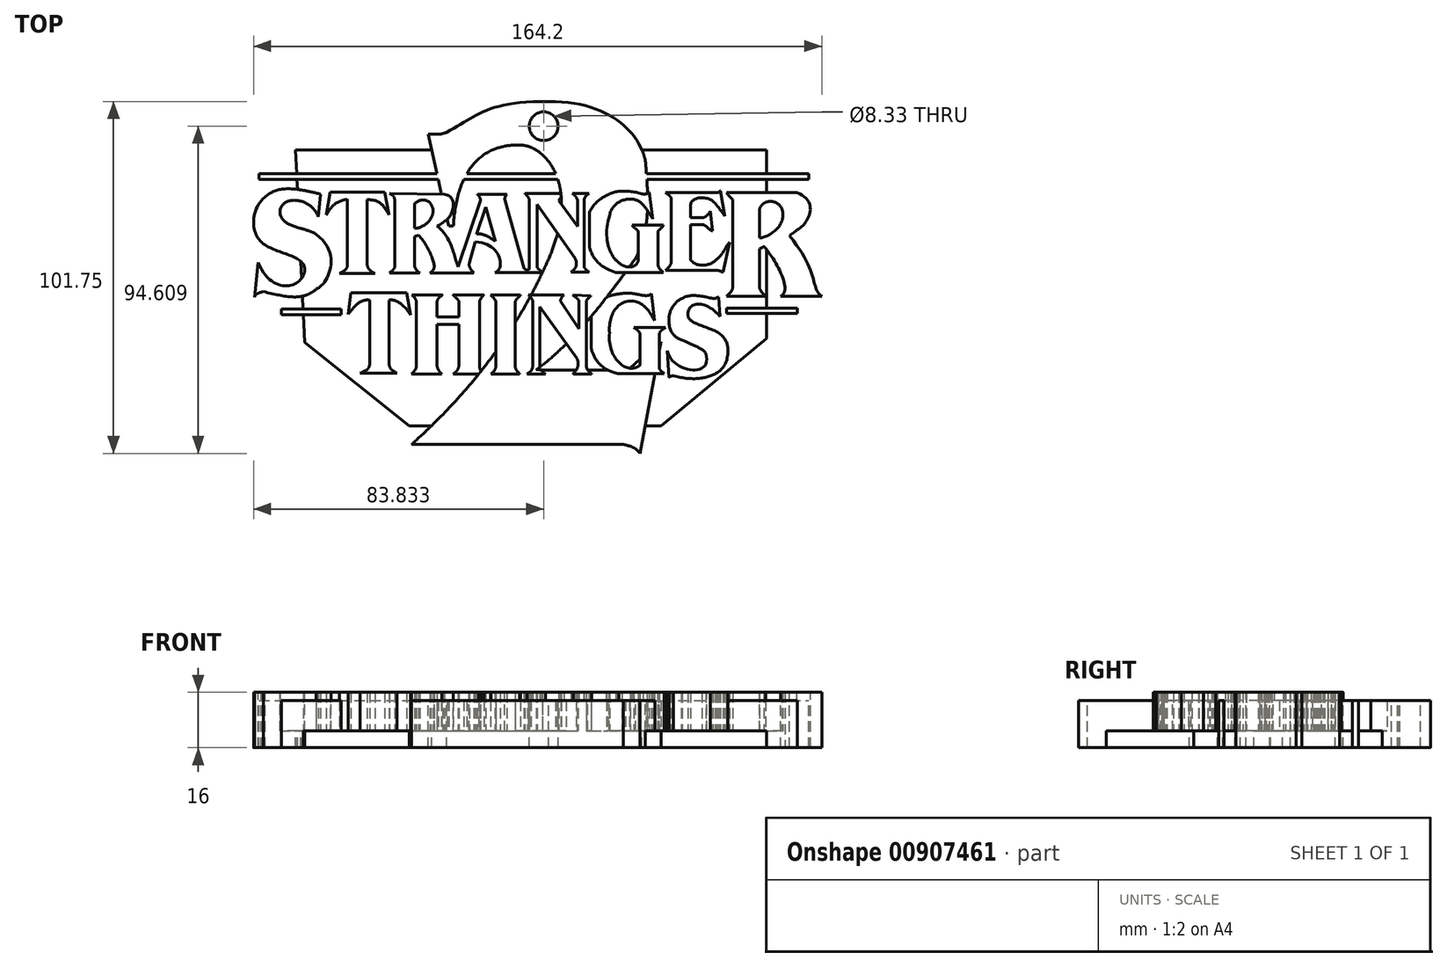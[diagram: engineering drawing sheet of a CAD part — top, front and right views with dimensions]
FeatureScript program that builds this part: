
annotation { "Feature Type Name" : "Feature", "Feature Type Description" : "" }
export const myFeature = defineFeature(function(context is Context, id is Id, definition is map)
    precondition{}
    {
        {
            var Q0;
            Q0=qCreatedBy(makeId("Top.planeOp"),FACE);
            var sketch = newSketch(context, id + "F0", { "sketchPlane" : qUnion([Q0])});
            skLineSegment(sketch, "E0", {"start": v(-115.56, -14.61) * mm, "end": v(-98.36, -14.61) * mm});
            skLineSegment(sketch, "E1", {"start": v(-98.36, -14.61) * mm, "end": v(-98.36, -16.18) * mm});
            skLineSegment(sketch, "E2", {"start": v(-98.36, -16.18) * mm, "end": v(-115.56, -16.18) * mm});
            skLineSegment(sketch, "E3", {"start": v(-115.56, -16.18) * mm, "end": v(-115.56, -14.61) * mm});
            skLineSegment(sketch, "E4", {"start": v(13.08, -14.33) * mm, "end": v(33.45, -14.33) * mm});
            skLineSegment(sketch, "E5", {"start": v(33.45, -14.33) * mm, "end": v(33.45, -15.84) * mm});
            skLineSegment(sketch, "E6", {"start": v(33.45, -15.84) * mm, "end": v(13.08, -15.84) * mm});
            skLineSegment(sketch, "E7", {"start": v(13.08, -15.84) * mm, "end": v(13.08, -14.33) * mm});
            skLineSegment(sketch, "E8", {"start": v(-122.08, 24.56) * mm, "end": v(36.78, 24.56) * mm});
            skLineSegment(sketch, "E9", {"start": v(36.78, 24.56) * mm, "end": v(36.78, 22.85) * mm});
            skLineSegment(sketch, "E10", {"start": v(-122.08, 24.56) * mm, "end": v(-122.08, 22.85) * mm});
            skLineSegment(sketch, "E11", {"start": v(-122.08, 22.85) * mm, "end": v(36.78, 22.85) * mm});
            skLineSegment(sketch, "E12", {"start": v(-104.27, 18.6) * mm, "end": v(-104.97, 12.15) * mm});
            skLineSegment(sketch, "E13", {"start": v(-122.33, -1.1) * mm, "end": v(-123.42, -11.13) * mm});
            skFitSpline(sketch, "E14", {"points": [v(-104.97, 12.15) * mm, v(-116.03, 13.12) * mm], "startDerivative": vector(-6.7, 17.7) * mm, "endDerivative": vector(0.72, -16.02) * mm});
            skFitSpline(sketch, "E15", {"points": [v(-116.03, 13.12) * mm, v(-105.51, 6.98) * mm], "startDerivative": vector(1.67, -13.15) * mm, "endDerivative": vector(7.41, -5.98) * mm});
            skFitSpline(sketch, "E16", {"points": [v(-105.51, 6.98) * mm, v(-105.51, -8.8) * mm], "startDerivative": vector(24.39, -18.65) * mm, "endDerivative": vector(-7.65, -2.15) * mm});
            skFitSpline(sketch, "E17", {"points": [v(-105.51, -8.8) * mm, v(-120.85, -9.54) * mm], "startDerivative": vector(-12.11, -10.3) * mm, "endDerivative": vector(-21.47, 5.07) * mm});
            skFitSpline(sketch, "E18", {"points": [v(-120.85, -9.54) * mm, v(-123.42, -11.13) * mm], "startDerivative": vector(-7.42, -2.2) * mm, "endDerivative": vector(-1.78, -2.6) * mm});
            skFitSpline(sketch, "E19", {"points": [v(-122.33, -1.1) * mm, v(-109.2, -1.71) * mm], "startDerivative": vector(14.98, -35.29) * mm, "endDerivative": vector(-6.9, 15.5) * mm});
            skFitSpline(sketch, "E20", {"points": [v(-109.2, -1.71) * mm, v(-121.46, 4.84) * mm], "startDerivative": vector(-5.57, 9.15) * mm, "endDerivative": vector(-7.89, 8.6) * mm});
            skFitSpline(sketch, "E21", {"points": [v(-121.46, 4.84) * mm, v(-120.34, 17.83) * mm], "startDerivative": vector(-8.13, 7.77) * mm, "endDerivative": vector(13.87, 12.55) * mm});
            skFitSpline(sketch, "E22", {"points": [v(-120.34, 17.83) * mm, v(-104.27, 18.6) * mm], "startDerivative": vector(9.93, 8.5) * mm, "endDerivative": vector(27.3, -7) * mm});
            skLineSegment(sketch, "E23", {"start": v(-101.46, 19.26) * mm, "end": v(-102.62, 12.63) * mm});
            skLineSegment(sketch, "E24", {"start": v(-101.46, 19.26) * mm, "end": v(-85.78, 19.26) * mm});
            skLineSegment(sketch, "E25", {"start": v(-85.78, 19.26) * mm, "end": v(-84.5, 12.63) * mm});
            skLineSegment(sketch, "E26", {"start": v(-98.83, -4.31) * mm, "end": v(-88.55, -4.31) * mm});
            skLineSegment(sketch, "E27", {"start": v(-90.78, 17.02) * mm, "end": v(-90.78, -1.86) * mm});
            skLineSegment(sketch, "E28", {"start": v(-96.53, 17.13) * mm, "end": v(-96.53, -1.86) * mm});
            skFitSpline(sketch, "E29", {"points": [v(-96.53, 17.13) * mm, v(-102.62, 12.63) * mm], "startDerivative": vector(-9.64, -1.52) * mm, "endDerivative": vector(-4.74, -8.43) * mm});
            skFitSpline(sketch, "E30", {"points": [v(-90.78, 17.02) * mm, v(-84.5, 12.63) * mm], "startDerivative": vector(9.13, 0) * mm, "endDerivative": vector(5.98, -10.96) * mm});
            skFitSpline(sketch, "E31", {"points": [v(-96.53, -1.86) * mm, v(-98.83, -4.31) * mm], "startDerivative": vector(-0.34, -4.23) * mm, "endDerivative": vector(-3.35, -1.95) * mm});
            skFitSpline(sketch, "E32", {"points": [v(-90.78, -1.86) * mm, v(-88.55, -4.31) * mm], "startDerivative": vector(0.68, -3.89) * mm, "endDerivative": vector(3.48, -1.95) * mm});
            skLineSegment(sketch, "E33", {"start": v(-84.38, -4.12) * mm, "end": v(-75.62, -4.12) * mm});
            skLineSegment(sketch, "E34", {"start": v(-82.8, 16.9) * mm, "end": v(-82.8, -2.26) * mm});
            skLineSegment(sketch, "E35", {"start": v(-77.1, 6.42) * mm, "end": v(-77.1, -2.26) * mm});
            skLineSegment(sketch, "E36", {"start": v(-84.32, 18.83) * mm, "end": v(-68.44, 18.56) * mm});
            skLineSegment(sketch, "E37", {"start": v(-72.63, -4.12) * mm, "end": v(-59.95, -4.12) * mm});
            skLineSegment(sketch, "E38", {"start": v(-58.03, 16.82) * mm, "end": v(-64.53, -2.34) * mm});
            skLineSegment(sketch, "E39", {"start": v(-58.97, 18.56) * mm, "end": v(-50.48, 18.56) * mm});
            skLineSegment(sketch, "E40", {"start": v(-51, 16.82) * mm, "end": v(-45.54, -2.74) * mm});
            skLineSegment(sketch, "E41", {"start": v(-56.57, 14.86) * mm, "end": v(-53.74, 4.93) * mm});
            skLineSegment(sketch, "E42", {"start": v(-56.57, 14.86) * mm, "end": v(-59.22, 7.05) * mm});
            skLineSegment(sketch, "E43", {"start": v(-77.1, 15.79) * mm, "end": v(-77.1, 8.77) * mm});
            skLineSegment(sketch, "E44", {"start": v(-77.1, 6.42) * mm, "end": v(-75.95, 6.75) * mm});
            skFitSpline(sketch, "E45", {"points": [v(-82.8, 16.9) * mm, v(-84.32, 18.83) * mm], "startDerivative": vector(-0.68, 1.63) * mm, "endDerivative": vector(-4.46, 2.16) * mm});
            skFitSpline(sketch, "E46", {"points": [v(-82.8, -2.26) * mm, v(-84.38, -4.12) * mm], "startDerivative": vector(-0.52, -2.38) * mm, "endDerivative": vector(-2.53, -1.68) * mm});
            skFitSpline(sketch, "E47", {"points": [v(-77.1, -2.26) * mm, v(-75.62, -4.12) * mm], "startDerivative": vector(0.5, -1.88) * mm, "endDerivative": vector(1.96, -0.98) * mm});
            skFitSpline(sketch, "E48", {"points": [v(-72.63, -4.12) * mm, v(-71.48, -2.45) * mm], "startDerivative": vector(1.67, 1.42) * mm, "endDerivative": vector(-0.12, 2.27) * mm});
            skFitSpline(sketch, "E49", {"points": [v(-75.95, 6.75) * mm, v(-71.48, -2.45) * mm], "startDerivative": vector(7.56, -7.63) * mm, "endDerivative": vector(-0.72, -4.54) * mm});
            skFitSpline(sketch, "E50", {"points": [v(-77.1, 15.79) * mm, v(-72.38, 15.79) * mm], "startDerivative": vector(3.65, 4.84) * mm, "endDerivative": vector(2.79, -4.3) * mm});
            skFitSpline(sketch, "E51", {"points": [v(-72.38, 15.79) * mm, v(-72.38, 11.78) * mm], "startDerivative": vector(3.38, -5.66) * mm, "endDerivative": vector(-1.01, -1.44) * mm});
            skFitSpline(sketch, "E52", {"points": [v(-72.38, 11.78) * mm, v(-77.1, 8.77) * mm], "startDerivative": vector(-2.03, -5.66) * mm, "endDerivative": vector(-2.78, 0.77) * mm});
            skFitSpline(sketch, "E53", {"points": [v(-68.44, 18.56) * mm, v(-68.44, 10.83) * mm], "startDerivative": vector(13.03, -1.77) * mm, "endDerivative": vector(-6.4, -1.9) * mm});
            skFitSpline(sketch, "E54", {"points": [v(-68.44, 10.83) * mm, v(-70.6, 9.42) * mm], "startDerivative": vector(-1.85, -1.4) * mm, "endDerivative": vector(-2.61, -1) * mm});
            skFitSpline(sketch, "E55", {"points": [v(-70.6, 9.42) * mm, v(-64.53, -2.34) * mm], "startDerivative": vector(13.18, -10.54) * mm, "endDerivative": vector(3.83, -8.97) * mm});
            skFitSpline(sketch, "E56", {"points": [v(-58.97, 18.56) * mm, v(-58.03, 16.82) * mm], "startDerivative": vector(1.45, -1.2) * mm, "endDerivative": vector(0.22, -1.95) * mm});
            skFitSpline(sketch, "E57", {"points": [v(-50.48, 18.56) * mm, v(-51, 16.82) * mm], "startDerivative": vector(-1.16, -1.38) * mm, "endDerivative": vector(0.54, -1.95) * mm});
            skFitSpline(sketch, "E58", {"points": [v(-59.22, 7.05) * mm, v(-53.74, 4.93) * mm], "startDerivative": vector(5.56, 1.31) * mm, "endDerivative": vector(3.71, -3.01) * mm});
            skLineSegment(sketch, "E59", {"start": v(-59.58, 4.83) * mm, "end": v(-61.27, -1.15) * mm});
            skFitSpline(sketch, "E60", {"points": [v(-61.27, -1.15) * mm, v(-59.95, -4.12) * mm], "startDerivative": vector(-0.85, -4.56) * mm, "endDerivative": vector(2.53, -2.66) * mm});
            skFitSpline(sketch, "E61", {"points": [v(-59.58, 4.83) * mm, v(-53.86, -4.02) * mm], "startDerivative": vector(23.16, -0.93) * mm, "endDerivative": vector(-8.7, -2.62) * mm});
            skLineSegment(sketch, "E62", {"start": v(-53.86, -4.02) * mm, "end": v(-39.82, -4.02) * mm});
            skFitSpline(sketch, "E63", {"points": [v(-45.54, -2.74) * mm, v(-44.46, -3.33) * mm], "startDerivative": vector(1.13, -1.2) * mm, "endDerivative": vector(0.96, 0.06) * mm});
            skLineSegment(sketch, "E64", {"start": v(-43.95, 16.82) * mm, "end": v(-43.95, -2.74) * mm});
            skLineSegment(sketch, "E65", {"start": v(-41.7, 15.7) * mm, "end": v(-41.7, -2.56) * mm});
            skLineSegment(sketch, "E66", {"start": v(-41.7, 15.7) * mm, "end": v(-30.82, 0.2) * mm});
            skLineSegment(sketch, "E67", {"start": v(-28.13, 16.82) * mm, "end": v(-28.13, -2.24) * mm});
            skLineSegment(sketch, "E68", {"start": v(-30, 9.36) * mm, "end": v(-30, 16.82) * mm});
            skLineSegment(sketch, "E69", {"start": v(-30, 9.36) * mm, "end": v(-35.43, 16.82) * mm});
            skLineSegment(sketch, "E70", {"start": v(-31.9, -3.91) * mm, "end": v(-26.69, -3.91) * mm});
            skFitSpline(sketch, "E71", {"points": [v(-45.3, 18.8) * mm, v(-43.95, 16.82) * mm], "startDerivative": vector(2.33, -1.66) * mm, "endDerivative": vector(0.16, -2.02) * mm});
            skLineSegment(sketch, "E72", {"start": v(-45.3, 18.8) * mm, "end": v(-33.67, 18.8) * mm});
            skLineSegment(sketch, "E73", {"start": v(-31.48, 18.82) * mm, "end": v(-26.71, 18.82) * mm});
            skFitSpline(sketch, "E74", {"points": [v(-33.67, 18.8) * mm, v(-35.43, 16.82) * mm], "startDerivative": vector(-2.14, -1.4) * mm, "endDerivative": vector(-1.4, -2.64) * mm});
            skFitSpline(sketch, "E75", {"points": [v(-31.48, 18.82) * mm, v(-30, 16.82) * mm], "startDerivative": vector(2.62, -1.89) * mm, "endDerivative": vector(0.61, -2.1) * mm});
            skFitSpline(sketch, "E76", {"points": [v(-26.71, 18.82) * mm, v(-28.13, 16.82) * mm], "startDerivative": vector(-2.63, -1.38) * mm, "endDerivative": vector(0.07, -1.93) * mm});
            skFitSpline(sketch, "E77", {"points": [v(-41.7, -2.56) * mm, v(-39.82, -4.02) * mm], "startDerivative": vector(0.99, -1.84) * mm, "endDerivative": vector(2.93, -1.74) * mm});
            skFitSpline(sketch, "E78", {"points": [v(-43.95, -2.74) * mm, v(-44.46, -3.33) * mm], "startDerivative": vector(-0.17, -0.85) * mm, "endDerivative": vector(-1.15, -0.18) * mm});
            skFitSpline(sketch, "E79", {"points": [v(-30.82, 0.2) * mm, v(-31.9, -3.91) * mm], "startDerivative": vector(3.02, -5.04) * mm, "endDerivative": vector(-4.17, -2.33) * mm});
            skFitSpline(sketch, "E80", {"points": [v(-28.13, -2.24) * mm, v(-26.69, -3.91) * mm], "startDerivative": vector(-0.04, -1.5) * mm, "endDerivative": vector(2.15, -1.54) * mm});
            skLineSegment(sketch, "E81", {"start": v(-26.62, 13.32) * mm, "end": v(-26.62, 3.3) * mm});
            skLineSegment(sketch, "E82", {"start": v(-9.32, 19.26) * mm, "end": v(-8.26, 11.44) * mm});
            skLineSegment(sketch, "E83", {"start": v(-14.21, 9.64) * mm, "end": v(-5.2, 9.64) * mm});
            skLineSegment(sketch, "E84", {"start": v(-12.45, 7.76) * mm, "end": v(-12.45, -0.6) * mm});
            skLineSegment(sketch, "E85", {"start": v(-6.75, 7.76) * mm, "end": v(-6.75, -0.44) * mm});
            skLineSegment(sketch, "E86", {"start": v(-5.24, -4) * mm, "end": v(-18.99, -4) * mm});
            skFitSpline(sketch, "E87", {"points": [v(-9.32, 19.26) * mm, v(-11.08, 18.65) * mm], "startDerivative": vector(-0.62, -0.71) * mm, "endDerivative": vector(-3.53, 0.36) * mm});
            skFitSpline(sketch, "E88", {"points": [v(-11.08, 18.65) * mm, v(-20.77, 18.65) * mm], "startDerivative": vector(-8.87, 2.65) * mm, "endDerivative": vector(-7.05, -3.96) * mm});
            skFitSpline(sketch, "E89", {"points": [v(-20.77, 18.65) * mm, v(-26.62, 13.32) * mm], "startDerivative": vector(-2.87, -0.82) * mm, "endDerivative": vector(-4.52, -10.13) * mm});
            skFitSpline(sketch, "E90", {"points": [v(-26.62, 3.3) * mm, v(-18.99, -4) * mm], "startDerivative": vector(3.4, -9.95) * mm, "endDerivative": vector(15.5, -5.37) * mm});
            skFitSpline(sketch, "E91", {"points": [v(-6.75, -0.44) * mm, v(-5.24, -4) * mm], "startDerivative": vector(-0.52, -4.85) * mm, "endDerivative": vector(4.26, -3.28) * mm});
            skFitSpline(sketch, "E92", {"points": [v(-5.2, 9.64) * mm, v(-6.75, 7.76) * mm], "startDerivative": vector(-1.06, -2.75) * mm, "endDerivative": vector(0.34, -1.3) * mm});
            skFitSpline(sketch, "E93", {"points": [v(-14.21, 9.64) * mm, v(-12.45, 7.76) * mm], "startDerivative": vector(0.86, -2.25) * mm, "endDerivative": vector(0.73, -2.3) * mm});
            skFitSpline(sketch, "E94", {"points": [v(-8.26, 11.44) * mm, v(-14.88, 17.22) * mm], "startDerivative": vector(-5.8, 8.8) * mm, "endDerivative": vector(-9.98, -0.32) * mm});
            skFitSpline(sketch, "E95", {"points": [v(-14.88, 17.22) * mm, v(-20.76, 12.53) * mm], "startDerivative": vector(-7.68, -0.28) * mm, "endDerivative": vector(-1.7, -9.38) * mm});
            skFitSpline(sketch, "E96", {"points": [v(-20.76, 12.53) * mm, v(-18.63, -0.74) * mm], "startDerivative": vector(-6.82, -21.18) * mm, "endDerivative": vector(4.98, -4.12) * mm});
            skFitSpline(sketch, "E97", {"points": [v(-18.63, -0.74) * mm, v(-12.45, -0.6) * mm], "startDerivative": vector(7.1, -7.4) * mm, "endDerivative": vector(1.75, 6.66) * mm});
            skLineSegment(sketch, "E98", {"start": v(-4.6, 19.07) * mm, "end": v(10.35, 19.07) * mm});
            skLineSegment(sketch, "E99", {"start": v(-3, 17.52) * mm, "end": v(-3, -1.24) * mm});
            skLineSegment(sketch, "E100", {"start": v(2.69, 11.79) * mm, "end": v(2.69, 15.63) * mm});
            skLineSegment(sketch, "E101", {"start": v(2.69, 11.79) * mm, "end": v(5.9, 11.79) * mm});
            skLineSegment(sketch, "E102", {"start": v(2.69, 9.85) * mm, "end": v(5.86, 9.85) * mm});
            skLineSegment(sketch, "E103", {"start": v(2.69, 9.85) * mm, "end": v(2.69, -0.44) * mm});
            skLineSegment(sketch, "E104", {"start": v(-4.57, -3.38) * mm, "end": v(9.75, -3.38) * mm});
            skLineSegment(sketch, "E105", {"start": v(13.87, 4.73) * mm, "end": v(12, -3.96) * mm});
            skLineSegment(sketch, "E106", {"start": v(12.56, 12.24) * mm, "end": v(11.2, 19.63) * mm});
            skFitSpline(sketch, "E107", {"points": [v(10.35, 19.07) * mm, v(11.2, 19.63) * mm], "startDerivative": vector(1.3, 0.11) * mm, "endDerivative": vector(0.57, 0.76) * mm});
            skFitSpline(sketch, "E108", {"points": [v(9.75, -3.38) * mm, v(12, -3.96) * mm], "startDerivative": vector(2.64, -0.07) * mm, "endDerivative": vector(2, -1.18) * mm});
            skFitSpline(sketch, "E109", {"points": [v(-3, -1.24) * mm, v(-4.57, -3.38) * mm], "startDerivative": vector(-0.34, -2.4) * mm, "endDerivative": vector(-2.1, -2.14) * mm});
            skFitSpline(sketch, "E110", {"points": [v(-3, 17.52) * mm, v(-4.6, 19.07) * mm], "startDerivative": vector(-0.41, 1.56) * mm, "endDerivative": vector(-2.56, 1.83) * mm});
            skLineSegment(sketch, "E111", {"start": v(8.36, 13.7) * mm, "end": v(8.93, 8.01) * mm});
            skFitSpline(sketch, "E112", {"points": [v(5.9, 11.79) * mm, v(8.36, 13.7) * mm], "startDerivative": vector(3.05, 0.1) * mm, "endDerivative": vector(1.5, 2.63) * mm});
            skFitSpline(sketch, "E113", {"points": [v(5.86, 9.85) * mm, v(8.93, 8.01) * mm], "startDerivative": vector(4.1, 0.04) * mm, "endDerivative": vector(3.03, -0.5) * mm});
            skFitSpline(sketch, "E114", {"points": [v(2.69, 15.63) * mm, v(9.98, 15.63) * mm], "startDerivative": vector(0, 6.72) * mm, "endDerivative": vector(6.11, -9) * mm});
            skFitSpline(sketch, "E115", {"points": [v(9.98, 15.63) * mm, v(12.56, 12.24) * mm], "startDerivative": vector(3.13, -3.8) * mm, "endDerivative": vector(2.62, -4.1) * mm});
            skFitSpline(sketch, "E116", {"points": [v(2.69, -0.44) * mm, v(9.87, -0.44) * mm], "startDerivative": vector(6.27, -7.21) * mm, "endDerivative": vector(4.23, 4.6) * mm});
            skFitSpline(sketch, "E117", {"points": [v(9.87, -0.44) * mm, v(13.87, 4.73) * mm], "startDerivative": vector(5.83, 3.78) * mm, "endDerivative": vector(4, 5.17) * mm});
            skLineSegment(sketch, "E118", {"start": v(14.87, 16.68) * mm, "end": v(14.87, -7.95) * mm});
            skLineSegment(sketch, "E119", {"start": v(13.06, -10.87) * mm, "end": v(24.3, -10.87) * mm});
            skLineSegment(sketch, "E120", {"start": v(28.65, -10.87) * mm, "end": v(40.55, -10.87) * mm});
            skLineSegment(sketch, "E121", {"start": v(22.59, 2.83) * mm, "end": v(22.59, -7.79) * mm});
            skLineSegment(sketch, "E122", {"start": v(13.08, 19.11) * mm, "end": v(33.42, 19.11) * mm});
            skLineSegment(sketch, "E123", {"start": v(22.6, 5.94) * mm, "end": v(22.6, 14.36) * mm});
            skLineSegment(sketch, "E124", {"start": v(22.59, 2.83) * mm, "end": v(23.86, 3.49) * mm});
            skFitSpline(sketch, "E125", {"points": [v(13.06, -10.87) * mm, v(14.87, -7.95) * mm], "startDerivative": vector(3.62, 3.44) * mm, "endDerivative": vector(0.1, 3.6) * mm});
            skFitSpline(sketch, "E126", {"points": [v(22.59, -7.79) * mm, v(24.3, -10.87) * mm], "startDerivative": vector(-0.63, -4.1) * mm, "endDerivative": vector(2.73, -2.94) * mm});
            skFitSpline(sketch, "E127", {"points": [v(13.08, 19.11) * mm, v(14.87, 16.68) * mm], "startDerivative": vector(1.42, -3.5) * mm, "endDerivative": vector(0.04, -2.01) * mm});
            skFitSpline(sketch, "E128", {"points": [v(22.6, 14.36) * mm, v(29.06, 14.36) * mm], "startDerivative": vector(2.12, 7.52) * mm, "endDerivative": vector(4.9, -9.89) * mm});
            skFitSpline(sketch, "E129", {"points": [v(29.06, 14.36) * mm, v(22.6, 5.94) * mm], "startDerivative": vector(4.9, -15.98) * mm, "endDerivative": vector(-6.18, -0.5) * mm});
            skFitSpline(sketch, "E130", {"points": [v(33.42, 19.11) * mm, v(33.42, 8.24) * mm], "startDerivative": vector(19.88, -8.42) * mm, "endDerivative": vector(-9.9, -5.41) * mm});
            skFitSpline(sketch, "E131", {"points": [v(33.42, 8.24) * mm, v(31.2, 6.61) * mm], "startDerivative": vector(-1.93, -1.52) * mm, "endDerivative": vector(-2.22, -1.63) * mm});
            skFitSpline(sketch, "E132", {"points": [v(31.2, 6.61) * mm, v(40.55, -10.87) * mm], "startDerivative": vector(27.09, -33) * mm, "endDerivative": vector(10.76, -8.27) * mm});
            skFitSpline(sketch, "E133", {"points": [v(23.86, 3.49) * mm, v(28.65, -10.87) * mm], "startDerivative": vector(3.81, -3.35) * mm, "endDerivative": vector(-12.58, -6.4) * mm});
            skLineSegment(sketch, "E134", {"start": v(-95.5, -9.84) * mm, "end": v(-79.43, -9.84) * mm});
            skLineSegment(sketch, "E135", {"start": v(-95.5, -9.84) * mm, "end": v(-96.34, -16.16) * mm});
            skLineSegment(sketch, "E136", {"start": v(-79.43, -9.84) * mm, "end": v(-78.25, -16.38) * mm});
            skLineSegment(sketch, "E137", {"start": v(-84.45, -11.99) * mm, "end": v(-84.45, -30.75) * mm});
            skLineSegment(sketch, "E138", {"start": v(-90.14, -11.99) * mm, "end": v(-90.14, -30.75) * mm});
            skLineSegment(sketch, "E139", {"start": v(-92.8, -33.15) * mm, "end": v(-82.15, -33.15) * mm});
            skFitSpline(sketch, "E140", {"points": [v(-90.14, -11.99) * mm, v(-96.34, -16.16) * mm], "startDerivative": vector(-9.43, 0.92) * mm, "endDerivative": vector(-4.75, -5.99) * mm});
            skFitSpline(sketch, "E141", {"points": [v(-84.45, -11.99) * mm, v(-78.25, -16.38) * mm], "startDerivative": vector(6.27, 1.32) * mm, "endDerivative": vector(4.29, -7.67) * mm});
            skFitSpline(sketch, "E142", {"points": [v(-90.14, -30.75) * mm, v(-92.8, -33.15) * mm], "startDerivative": vector(-1.11, -3.7) * mm, "endDerivative": vector(-6.9, -3.49) * mm});
            skFitSpline(sketch, "E143", {"points": [v(-84.45, -30.75) * mm, v(-82.15, -33.15) * mm], "startDerivative": vector(0.58, -3.58) * mm, "endDerivative": vector(3.21, -1.82) * mm});
            skLineSegment(sketch, "E144", {"start": v(-77.94, -10.5) * mm, "end": v(-69, -10.5) * mm});
            skLineSegment(sketch, "E145", {"start": v(-76.62, -12.24) * mm, "end": v(-76.62, -31.2) * mm});
            skLineSegment(sketch, "E146", {"start": v(-70.6, -12.24) * mm, "end": v(-70.6, -16.84) * mm});
            skLineSegment(sketch, "E147", {"start": v(-70.6, -16.84) * mm, "end": v(-64.35, -16.84) * mm});
            skLineSegment(sketch, "E148", {"start": v(-64.35, -12.24) * mm, "end": v(-64.35, -16.84) * mm});
            skLineSegment(sketch, "E149", {"start": v(-66.11, -10.5) * mm, "end": v(-57.1, -10.5) * mm});
            skLineSegment(sketch, "E150", {"start": v(-58.33, -12.24) * mm, "end": v(-58.33, -31.15) * mm});
            skLineSegment(sketch, "E151", {"start": v(-70.6, -18.97) * mm, "end": v(-70.6, -31.15) * mm});
            skLineSegment(sketch, "E152", {"start": v(-70.6, -18.97) * mm, "end": v(-64.35, -18.97) * mm});
            skLineSegment(sketch, "E153", {"start": v(-64.35, -18.97) * mm, "end": v(-64.35, -31.15) * mm});
            skLineSegment(sketch, "E154", {"start": v(-78.04, -33.34) * mm, "end": v(-69.22, -33.34) * mm});
            skLineSegment(sketch, "E155", {"start": v(-65.9, -33.34) * mm, "end": v(-57.27, -33.34) * mm});
            skFitSpline(sketch, "E156", {"points": [v(-77.94, -10.5) * mm, v(-76.62, -12.24) * mm], "startDerivative": vector(2.46, -1.68) * mm, "endDerivative": vector(0.81, -1.74) * mm});
            skFitSpline(sketch, "E157", {"points": [v(-69, -10.5) * mm, v(-70.6, -12.24) * mm], "startDerivative": vector(-2.14, -1.42) * mm, "endDerivative": vector(-0.49, -2.04) * mm});
            skFitSpline(sketch, "E158", {"points": [v(-66.11, -10.5) * mm, v(-64.35, -12.24) * mm], "startDerivative": vector(2.2, -1.53) * mm, "endDerivative": vector(1.4, -2.01) * mm});
            skFitSpline(sketch, "E159", {"points": [v(-57.1, -10.5) * mm, v(-58.33, -12.24) * mm], "startDerivative": vector(-1.66, -1.31) * mm, "endDerivative": vector(-0.9, -1.65) * mm});
            skFitSpline(sketch, "E160", {"points": [v(-76.62, -31.2) * mm, v(-78.04, -33.34) * mm], "startDerivative": vector(-0.22, -2.46) * mm, "endDerivative": vector(-2.68, -2.33) * mm});
            skFitSpline(sketch, "E161", {"points": [v(-70.6, -31.15) * mm, v(-69.22, -33.34) * mm], "startDerivative": vector(0.7, -2.89) * mm, "endDerivative": vector(2.67, -2.25) * mm});
            skFitSpline(sketch, "E162", {"points": [v(-64.35, -31.15) * mm, v(-65.9, -33.34) * mm], "startDerivative": vector(-0.5, -3) * mm, "endDerivative": vector(-2.61, -1.95) * mm});
            skFitSpline(sketch, "E163", {"points": [v(-58.33, -31.15) * mm, v(-57.27, -33.34) * mm], "startDerivative": vector(0.13, -2.45) * mm, "endDerivative": vector(2.34, -2.07) * mm});
            skLineSegment(sketch, "E164", {"start": v(-55.14, -10.5) * mm, "end": v(-46.48, -10.5) * mm});
            skLineSegment(sketch, "E165", {"start": v(-55.08, -33.34) * mm, "end": v(-46.75, -33.34) * mm});
            skLineSegment(sketch, "E166", {"start": v(-48.03, -12.38) * mm, "end": v(-48.03, -31.42) * mm});
            skLineSegment(sketch, "E167", {"start": v(-53.62, -12.38) * mm, "end": v(-53.62, -31.27) * mm});
            skFitSpline(sketch, "E168", {"points": [v(-55.14, -10.5) * mm, v(-53.62, -12.38) * mm], "startDerivative": vector(4.15, -4.08) * mm, "endDerivative": vector(1.03, -1.65) * mm});
            skFitSpline(sketch, "E169", {"points": [v(-46.48, -10.5) * mm, v(-48.03, -12.38) * mm], "startDerivative": vector(-1.47, -1.98) * mm, "endDerivative": vector(-1.23, -2.75) * mm});
            skFitSpline(sketch, "E170", {"points": [v(-48.03, -31.42) * mm, v(-46.75, -33.34) * mm], "startDerivative": vector(0.85, -2.63) * mm, "endDerivative": vector(1.65, -1.67) * mm});
            skFitSpline(sketch, "E171", {"points": [v(-53.62, -31.27) * mm, v(-55.08, -33.34) * mm], "startDerivative": vector(-0.57, -2.41) * mm, "endDerivative": vector(-3.13, -1.93) * mm});
            skLineSegment(sketch, "E172", {"start": v(-44.24, -10.5) * mm, "end": v(-33.98, -10.5) * mm});
            skLineSegment(sketch, "E173", {"start": v(-31.44, -10.5) * mm, "end": v(-26.15, -10.77) * mm});
            skLineSegment(sketch, "E174", {"start": v(-44.6, -33.34) * mm, "end": v(-39.29, -33.34) * mm});
            skLineSegment(sketch, "E175", {"start": v(-31.33, -33.34) * mm, "end": v(-25.9, -33.34) * mm});
            skLineSegment(sketch, "E176", {"start": v(-42.99, -12.27) * mm, "end": v(-42.99, -31.3) * mm});
            skLineSegment(sketch, "E177", {"start": v(-40.98, -31.3) * mm, "end": v(-40.98, -13.93) * mm});
            skLineSegment(sketch, "E178", {"start": v(-40.98, -13.93) * mm, "end": v(-30.18, -28.9) * mm});
            skLineSegment(sketch, "E179", {"start": v(-34.97, -12.27) * mm, "end": v(-29.56, -20.23) * mm});
            skLineSegment(sketch, "E180", {"start": v(-29.56, -20.23) * mm, "end": v(-29.56, -12.27) * mm});
            skLineSegment(sketch, "E181", {"start": v(-27.43, -12.27) * mm, "end": v(-27.43, -31.3) * mm});
            skFitSpline(sketch, "E182", {"points": [v(-44.24, -10.5) * mm, v(-42.99, -12.27) * mm], "startDerivative": vector(2.06, -1.78) * mm, "endDerivative": vector(0.65, -1.97) * mm});
            skFitSpline(sketch, "E183", {"points": [v(-33.98, -10.5) * mm, v(-34.97, -12.27) * mm], "startDerivative": vector(-1.9, -1.84) * mm, "endDerivative": vector(-0.1, -1.44) * mm});
            skFitSpline(sketch, "E184", {"points": [v(-31.44, -10.5) * mm, v(-29.56, -12.27) * mm], "startDerivative": vector(3.65, -2.55) * mm, "endDerivative": vector(0.54, -1.02) * mm});
            skFitSpline(sketch, "E185", {"points": [v(-26.15, -10.77) * mm, v(-27.43, -12.27) * mm], "startDerivative": vector(-1.8, -1.7) * mm, "endDerivative": vector(-0.18, -1.51) * mm});
            skFitSpline(sketch, "E186", {"points": [v(-42.99, -31.3) * mm, v(-44.6, -33.34) * mm], "startDerivative": vector(-0.46, -2.55) * mm, "endDerivative": vector(-3.5, -2.1) * mm});
            skFitSpline(sketch, "E187", {"points": [v(-40.98, -31.3) * mm, v(-39.29, -33.34) * mm], "startDerivative": vector(0.38, -2.62) * mm, "endDerivative": vector(3.61, -2.45) * mm});
            skFitSpline(sketch, "E188", {"points": [v(-30.18, -28.9) * mm, v(-31.33, -33.34) * mm], "startDerivative": vector(2.9, -7.29) * mm, "endDerivative": vector(-1.94, -2.35) * mm});
            skFitSpline(sketch, "E189", {"points": [v(-27.43, -31.3) * mm, v(-25.9, -33.34) * mm], "startDerivative": vector(0.57, -3) * mm, "endDerivative": vector(2.66, -2.04) * mm});
            skLineSegment(sketch, "E190", {"start": v(-8.65, -10.1) * mm, "end": v(-7.78, -17.82) * mm});
            skLineSegment(sketch, "E191", {"start": v(-26.12, -15.74) * mm, "end": v(-26.12, -25.82) * mm});
            skLineSegment(sketch, "E192", {"start": v(-13.74, -19.97) * mm, "end": v(-4.58, -19.97) * mm});
            skLineSegment(sketch, "E193", {"start": v(-4.96, -33.3) * mm, "end": v(-18.04, -33.3) * mm});
            skLineSegment(sketch, "E194", {"start": v(-6.4, -21.7) * mm, "end": v(-6.4, -31.67) * mm});
            skLineSegment(sketch, "E195", {"start": v(-11.92, -21.7) * mm, "end": v(-11.92, -30.72) * mm});
            skFitSpline(sketch, "E196", {"points": [v(-8.65, -10.1) * mm, v(-9.95, -10.68) * mm], "startDerivative": vector(-1.23, -1.35) * mm, "endDerivative": vector(-1.58, -0.06) * mm});
            skFitSpline(sketch, "E197", {"points": [v(-9.95, -10.68) * mm, v(-17.2, -10.1) * mm], "startDerivative": vector(-2.06, -0.89) * mm, "endDerivative": vector(-8.76, -1.69) * mm});
            skFitSpline(sketch, "E198", {"points": [v(-17.2, -10.1) * mm, v(-26.12, -15.74) * mm], "startDerivative": vector(-14.8, -1.75) * mm, "endDerivative": vector(-11.94, -13.45) * mm});
            skFitSpline(sketch, "E199", {"points": [v(-6.4, -31.67) * mm, v(-4.96, -33.3) * mm], "startDerivative": vector(0.75, -2.19) * mm, "endDerivative": vector(2.07, -2) * mm});
            skFitSpline(sketch, "E200", {"points": [v(-26.12, -25.82) * mm, v(-18.04, -33.3) * mm], "startDerivative": vector(1.65, -7) * mm, "endDerivative": vector(17.57, -3.6) * mm});
            skFitSpline(sketch, "E201", {"points": [v(-7.78, -17.82) * mm, v(-14.71, -12.23) * mm], "startDerivative": vector(-5.59, 8.83) * mm, "endDerivative": vector(-11.83, 0.68) * mm});
            skFitSpline(sketch, "E202", {"points": [v(-14.71, -12.23) * mm, v(-20.8, -21.47) * mm], "startDerivative": vector(-14.54, -0.85) * mm, "endDerivative": vector(1.02, -11.5) * mm});
            skFitSpline(sketch, "E203", {"points": [v(-20.8, -21.47) * mm, v(-11.92, -30.72) * mm], "startDerivative": vector(-2.13, -22.22) * mm, "endDerivative": vector(11.08, 9.68) * mm});
            skFitSpline(sketch, "E204", {"points": [v(-13.74, -19.97) * mm, v(-11.92, -21.7) * mm], "startDerivative": vector(2.96, -1.53) * mm, "endDerivative": vector(1.4, -2.3) * mm});
            skFitSpline(sketch, "E205", {"points": [v(-4.58, -19.97) * mm, v(-6.4, -21.7) * mm], "startDerivative": vector(-3.4, -1.7) * mm, "endDerivative": vector(-1.2, -2.7) * mm});
            skLineSegment(sketch, "E206", {"start": v(10.78, -11.08) * mm, "end": v(11.13, -16.7) * mm});
            skLineSegment(sketch, "E207", {"start": v(-4.08, -26.6) * mm, "end": v(-3.6, -34.35) * mm});
            skFitSpline(sketch, "E208", {"points": [v(-4.08, -26.6) * mm, v(7.01, -27.41) * mm], "startDerivative": vector(3.98, -19.48) * mm, "endDerivative": vector(-7.1, 21.75) * mm});
            skFitSpline(sketch, "E209", {"points": [v(-3.6, -34.35) * mm, v(-2.28, -33.88) * mm], "startDerivative": vector(1.06, 1.03) * mm, "endDerivative": vector(1.4, 0.03) * mm});
            skFitSpline(sketch, "E210", {"points": [v(-2.28, -33.88) * mm, v(8.33, -33.89) * mm], "startDerivative": vector(12.33, -3.43) * mm, "endDerivative": vector(7.74, 3.2) * mm});
            skFitSpline(sketch, "E211", {"points": [v(8.33, -33.89) * mm, v(13.42, -26.6) * mm], "startDerivative": vector(8.18, 2.43) * mm, "endDerivative": vector(-0.08, 13.27) * mm});
            skFitSpline(sketch, "E212", {"points": [v(13.42, -26.6) * mm, v(8.12, -20.28) * mm], "startDerivative": vector(0.3, 6.93) * mm, "endDerivative": vector(-12.65, 3.77) * mm});
            skFitSpline(sketch, "E213", {"points": [v(8.12, -20.28) * mm, v(1.87, -16.09) * mm], "startDerivative": vector(-13.86, 5.4) * mm, "endDerivative": vector(0, 5.97) * mm});
            skFitSpline(sketch, "E214", {"points": [v(1.87, -16.09) * mm, v(11.13, -16.7) * mm], "startDerivative": vector(0.07, 11.66) * mm, "endDerivative": vector(12.21, -14.53) * mm});
            skFitSpline(sketch, "E215", {"points": [v(10.78, -11.08) * mm, v(9.08, -11.55) * mm], "startDerivative": vector(-2.46, -0.8) * mm, "endDerivative": vector(-1.8, 0.3) * mm});
            skFitSpline(sketch, "E216", {"points": [v(9.08, -11.55) * mm, v(0.18, -11.55) * mm], "startDerivative": vector(-9.73, 2.3) * mm, "endDerivative": vector(-6.99, -4.5) * mm});
            skFitSpline(sketch, "E217", {"points": [v(0.18, -11.55) * mm, v(-3.57, -17.48) * mm], "startDerivative": vector(-7.24, -2.92) * mm, "endDerivative": vector(0.4, -6.23) * mm});
            skFitSpline(sketch, "E218", {"points": [v(-3.57, -17.48) * mm, v(-0.02, -23.5) * mm], "startDerivative": vector(-1, -11.96) * mm, "endDerivative": vector(4.83, -2.01) * mm});
            skFitSpline(sketch, "E219", {"points": [v(-0.02, -23.5) * mm, v(7.01, -27.41) * mm], "startDerivative": vector(14.75, -6.41) * mm, "endDerivative": vector(2.02, -3.85) * mm});
            skLineSegment(sketch, "E220", {"start": v(-78, -53.73) * mm, "end": v(-16.75, -53.73) * mm});
            skLineSegment(sketch, "E221", {"start": v(-11.92, -56.34) * mm, "end": v(-5.91, -23.93) * mm});
            skFitSpline(sketch, "E222", {"points": [v(-16.75, -53.73) * mm, v(-11.92, -56.34) * mm], "startDerivative": vector(7.72, -1.73) * mm, "endDerivative": vector(3.95, -5.06) * mm});
            skLineSegment(sketch, "E223", {"start": v(-73.25, 36) * mm, "end": v(-67.27, 9.47) * mm});
            skLineSegment(sketch, "E224", {"start": v(-67.27, 9.47) * mm, "end": v(-65.92, 9.44) * mm});
            skFitSpline(sketch, "E225", {"points": [v(-73.25, 36) * mm, v(-67.86, 36.48) * mm], "startDerivative": vector(5.82, -0.06) * mm, "endDerivative": vector(5.62, 2.33) * mm});
            skFitSpline(sketch, "E226", {"points": [v(-67.86, 36.48) * mm, v(-38.43, 45.4) * mm], "startDerivative": vector(25.37, 13.3) * mm, "endDerivative": vector(54.89, -0.4) * mm});
            skFitSpline(sketch, "E227", {"points": [v(-38.43, 45.4) * mm, v(-10.4, 28.08) * mm], "startDerivative": vector(53.75, 0.75) * mm, "endDerivative": vector(4.26, -23.31) * mm});
            skFitSpline(sketch, "E228", {"points": [v(-10.4, 28.08) * mm, v(-13.3, 0) * mm], "startDerivative": vector(2.12, -27.66) * mm, "endDerivative": vector(-13.96, -25.22) * mm});
            skPoint(sketch, "E229.1.internal.snap0", {"position": v(-41.94, -33.34) * mm});
            skFitSpline(sketch, "E229", {"points": [v(-13.3, 0) * mm, v(-41.94, -32.14) * mm], "startDerivative": vector(-25.2, -34.78) * mm, "endDerivative": vector(-32.8, -24.1) * mm});
            skFitSpline(sketch, "E230", {"points": [v(-41.94, -32.14) * mm, v(-15.44, -32.14) * mm], "startDerivative": vector(29.13, -0.8) * mm, "endDerivative": vector(26.5, 0) * mm});
            skLineSegment(sketch, "E231", {"start": v(-15.44, -32.14) * mm, "end": v(-5.91, -23.93) * mm});
            skFitSpline(sketch, "E232", {"points": [v(-65.92, 9.44) * mm, v(-46.6, 32.84) * mm], "startDerivative": vector(2.09, 32.81) * mm, "endDerivative": vector(44.4, -0.85) * mm});
            skFitSpline(sketch, "E233", {"points": [v(-46.6, 32.84) * mm, v(-39.02, -1.54) * mm], "startDerivative": vector(21.52, -0.33) * mm, "endDerivative": vector(-31.56, -68.14) * mm});
            skFitSpline(sketch, "E234", {"points": [v(-39.02, -1.54) * mm, v(-78, -53.73) * mm], "startDerivative": vector(-22.24, -48.66) * mm, "endDerivative": vector(-62.04, -55.89) * mm});
            skLineSegment(sketch, "E235", {"start": v(-111.51, 31.4) * mm, "end": v(24.63, 31.4) * mm});
            skLineSegment(sketch, "E236", {"start": v(24.63, 31.4) * mm, "end": v(24.63, -23.1) * mm});
            skLineSegment(sketch, "E237", {"start": v(24.63, -23.1) * mm, "end": v(-5.86, -48.31) * mm});
            skLineSegment(sketch, "E238", {"start": v(-5.86, -48.31) * mm, "end": v(-78.62, -48.31) * mm});
            skLineSegment(sketch, "E239", {"start": v(-78.62, -48.31) * mm, "end": v(-108.88, -24.28) * mm});
            skLineSegment(sketch, "E240", {"start": v(-108.88, -24.28) * mm, "end": v(-111.51, 31.4) * mm});
            skCircle(sketch, "E241", {"center": v(-39.82, 38.27) * mm, "radius": 4.16 * mm});
            skSolve(sketch);
        }
        {
            var Q0;
            {var subQ0=sQuery(id+"F0.wireOp",EDGE,"E240");var subQ1=sQuery(id+"F0.wireOp",EDGE,"E8");var subQ2=makeQuery(id+"F0.imprint","INTERSECT",VERTEX,{"derivedFrom":[subQ1,subQ0]});Q0=makeQuery(id+"F0.imprint","IMPRINT",FACE,{"disambiguationData":[TD([[makeQuery(id+"F0.imprint","IMPRINT",EDGE,{"disambiguationData":[TD([[subQ2,-1.0]])],"derivedFrom":subQ1}),1.0]])]});}
            var Q1;
            {var subQ0=sQuery(id+"F0.wireOp",EDGE,"E232");var subQ1=sQuery(id+"F0.wireOp",EDGE,"E8");var subQ2=makeQuery(id+"F0.imprint","INTERSECT",VERTEX,{"derivedFrom":[subQ1,subQ0]});Q1=makeQuery(id+"F0.imprint","IMPRINT",FACE,{"disambiguationData":[TD([[makeQuery(id+"F0.imprint","IMPRINT",EDGE,{"disambiguationData":[TD([[subQ2,-1.0]])],"derivedFrom":subQ1}),1.0]])]});}
            var Q2;
            {var subQ5=sQuery(id+"F0.wireOp",EDGE,"E236");var subQ7=sQuery(id+"F0.wireOp",EDGE,"E8");var subQ8=makeQuery(id+"F0.imprint","INTERSECT",VERTEX,{"derivedFrom":[subQ7,subQ5]});Q2=makeQuery(id+"F0.imprint","IMPRINT",FACE,{"disambiguationData":[TD([[makeQuery(id+"F0.imprint","IMPRINT",EDGE,{"disambiguationData":[TD([[subQ8,1.0]])],"derivedFrom":subQ7}),1.0]])]});}
            var Q3;
            {var subQ30=sQuery(id+"F0.wireOp",EDGE,"E7");Q3=makeQuery(id+"F0.imprint","IMPRINT",FACE,{"disambiguationData":[TD([[makeQuery(id+"F0.imprint","IMPRINT",EDGE,{"derivedFrom":subQ30}),1.0]])]});}
            var Q4;
            {var subQ5=sQuery(id+"F0.wireOp",EDGE,"E189");var subQ6=sQuery(id+"F0.wireOp",EDGE,"E181");var subQ7=makeQuery(id+"F0.imprint","INTERSECT",VERTEX,{"derivedFrom":[subQ6,subQ5]});Q4=makeQuery(id+"F0.imprint","IMPRINT",FACE,{"disambiguationData":[TD([[makeQuery(id+"F0.imprint","IMPRINT",EDGE,{"disambiguationData":[TD([[subQ7,1.0]])],"derivedFrom":subQ6}),1.0]])]});}
            var Q5;
            {var subQ1=sQuery(id+"F0.wireOp",EDGE,"E178");var subQ5=sQuery(id+"F0.wireOp",EDGE,"E188");var subQ6=makeQuery(id+"F0.imprint","INTERSECT",VERTEX,{"derivedFrom":[subQ1,subQ5]});Q5=makeQuery(id+"F0.imprint","IMPRINT",FACE,{"disambiguationData":[TD([[makeQuery(id+"F0.imprint","IMPRINT",EDGE,{"disambiguationData":[TD([[subQ6,1.0]])],"derivedFrom":subQ1}),-1.0]])]});}
            var Q6;
            {var subQ26=sQuery(id+"F0.wireOp",EDGE,"E1");Q6=makeQuery(id+"F0.imprint","IMPRINT",FACE,{"disambiguationData":[TD([[makeQuery(id+"F0.imprint","IMPRINT",EDGE,{"derivedFrom":subQ26}),1.0]])]});}
            var Q7;
            Q7=makeQuery(id+"F0.imprint","IMPRINT",FACE,{"disambiguationData":[TD([[makeQuery(id+"F0.imprint","IMPRINT",EDGE,{"derivedFrom":sQuery(id+"F0.wireOp",EDGE,"E38")}),-1.0]])]});
            var Q8;
            Q8=makeQuery(id+"F0.imprint","IMPRINT",FACE,{"disambiguationData":[TD([[makeQuery(id+"F0.imprint","IMPRINT",EDGE,{"derivedFrom":sQuery(id+"F0.wireOp",EDGE,"E43")}),1.0]])]});
            var Q9;
            Q9=makeQuery(id+"F0.imprint","IMPRINT",FACE,{"disambiguationData":[TD([[makeQuery(id+"F0.imprint","IMPRINT",EDGE,{"derivedFrom":sQuery(id+"F0.wireOp",EDGE,"E41")}),-1.0]])]});
            var Q10;
            {var subQ5=sQuery(id+"F0.wireOp",EDGE,"E65");Q10=makeQuery(id+"F0.imprint","IMPRINT",FACE,{"disambiguationData":[TD([[makeQuery(id+"F0.imprint","IMPRINT",EDGE,{"derivedFrom":subQ5}),1.0]])]});}
            var Q11;
            {var subQ0=sQuery(id+"F0.wireOp",EDGE,"E97");var subQ1=sQuery(id+"F0.wireOp",EDGE,"E84");var subQ2=makeQuery(id+"F0.imprint","INTERSECT",VERTEX,{"derivedFrom":[subQ1,subQ0]});Q11=makeQuery(id+"F0.imprint","IMPRINT",FACE,{"disambiguationData":[TD([[makeQuery(id+"F0.imprint","IMPRINT",EDGE,{"disambiguationData":[TD([[subQ2,1.0]])],"derivedFrom":subQ1}),-1.0]])]});}
            var Q12;
            {var subQ0=sQuery(id+"F0.wireOp",EDGE,"E74");var subQ1=sQuery(id+"F0.wireOp",EDGE,"E69");var subQ2=makeQuery(id+"F0.imprint","INTERSECT",VERTEX,{"derivedFrom":[subQ1,subQ0]});Q12=makeQuery(id+"F0.imprint","IMPRINT",FACE,{"disambiguationData":[TD([[makeQuery(id+"F0.imprint","IMPRINT",EDGE,{"disambiguationData":[TD([[subQ2,1.0]])],"derivedFrom":subQ1}),-1.0]])]});}
            var Q13;
            {var subQ0=sQuery(id+"F0.wireOp",EDGE,"E123");Q13=makeQuery(id+"F0.imprint","IMPRINT",FACE,{"disambiguationData":[TD([[makeQuery(id+"F0.imprint","IMPRINT",EDGE,{"derivedFrom":subQ0}),-1.0]])]});}
            var Q14;
            {var subQ0=sQuery(id+"F0.wireOp",EDGE,"E229");var subQ1=sQuery(id+"F0.wireOp",EDGE,"E187");var subQ2=makeQuery(id+"F0.imprint","INTERSECT",VERTEX,{"derivedFrom":[subQ1,subQ0]});Q14=makeQuery(id+"F0.imprint","IMPRINT",FACE,{"disambiguationData":[TD([[makeQuery(id+"F0.imprint","IMPRINT",EDGE,{"disambiguationData":[TD([[subQ2,-1.0]])],"derivedFrom":subQ1}),-1.0]])]});}
            var Q15;
            {var subQ0=sQuery(id+"F0.wireOp",EDGE,"E20");var subQ1=sQuery(id+"F0.wireOp",EDGE,"E19");var subQ2=makeQuery(id+"F0.imprint","INTERSECT",VERTEX,{"derivedFrom":[subQ1,subQ0]});Q15=makeQuery(id+"F0.imprint","IMPRINT",FACE,{"disambiguationData":[TD([[makeQuery(id+"F0.imprint","IMPRINT",EDGE,{"disambiguationData":[TD([[subQ2,1.0]])],"derivedFrom":subQ1}),1.0]])]});}
            var Q16;
            {var subQ0=sQuery(id+"F0.wireOp",EDGE,"E223");var subQ1=sQuery(id+"F0.wireOp",EDGE,"E8");var subQ2=makeQuery(id+"F0.imprint","INTERSECT",VERTEX,{"derivedFrom":[subQ1,subQ0]});Q16=makeQuery(id+"F0.imprint","IMPRINT",FACE,{"disambiguationData":[TD([[makeQuery(id+"F0.imprint","IMPRINT",EDGE,{"disambiguationData":[TD([[subQ2,-1.0]])],"derivedFrom":subQ1}),-1.0]])]});}
            var Q17;
            {var subQ4=sQuery(id+"F0.wireOp",EDGE,"E93");Q17=makeQuery(id+"F0.imprint","IMPRINT",FACE,{"disambiguationData":[TD([[makeQuery(id+"F0.imprint","IMPRINT",EDGE,{"derivedFrom":subQ4}),-1.0]])]});}
            var Q18;
            {var subQ0=sQuery(id+"F0.wireOp",EDGE,"E233");var subQ1=sQuery(id+"F0.wireOp",EDGE,"E8");var subQ2=makeQuery(id+"F0.imprint","INTERSECT",VERTEX,{"derivedFrom":[subQ1,subQ0]});Q18=makeQuery(id+"F0.imprint","IMPRINT",FACE,{"disambiguationData":[TD([[makeQuery(id+"F0.imprint","IMPRINT",EDGE,{"disambiguationData":[TD([[subQ2,-1.0]])],"derivedFrom":subQ1}),-1.0]])]});}
            var Q19;
            {var subQ0=sQuery(id+"F0.wireOp",EDGE,"E177");Q19=makeQuery(id+"F0.imprint","IMPRINT",FACE,{"disambiguationData":[TD([[makeQuery(id+"F0.imprint","IMPRINT",EDGE,{"derivedFrom":subQ0}),-1.0]])]});}
            var Q20;
            {var subQ0=sQuery(id+"F0.wireOp",EDGE,"E9");Q20=makeQuery(id+"F0.imprint","IMPRINT",FACE,{"disambiguationData":[TD([[makeQuery(id+"F0.imprint","IMPRINT",EDGE,{"derivedFrom":subQ0}),-1.0]])]});}
            var Q21;
            {var subQ0=sQuery(id+"F0.wireOp",EDGE,"E5");Q21=makeQuery(id+"F0.imprint","IMPRINT",FACE,{"disambiguationData":[TD([[makeQuery(id+"F0.imprint","IMPRINT",EDGE,{"derivedFrom":subQ0}),-1.0]])]});}
            var Q22;
            Q22=makeQuery(id+"F0.imprint","IMPRINT",FACE,{"disambiguationData":[TD([[makeQuery(id+"F0.imprint","IMPRINT",EDGE,{"derivedFrom":sQuery(id+"F0.wireOp",EDGE,"E173")}),-1.0]])]});
            var Q23;
            {var subQ10=sQuery(id+"F0.wireOp",EDGE,"E224");Q23=makeQuery(id+"F0.imprint","IMPRINT",FACE,{"disambiguationData":[TD([[makeQuery(id+"F0.imprint","IMPRINT",EDGE,{"derivedFrom":subQ10}),1.0]])]});}
            var Q24;
            Q24=makeQuery(id+"F0.imprint","IMPRINT",FACE,{"disambiguationData":[TD([[makeQuery(id+"F0.imprint","IMPRINT",EDGE,{"derivedFrom":sQuery(id+"F0.wireOp",EDGE,"E81")}),1.0]])]});
            var Q25;
            Q25=makeQuery(id+"F0.imprint","IMPRINT",FACE,{"disambiguationData":[TD([[makeQuery(id+"F0.imprint","IMPRINT",EDGE,{"derivedFrom":sQuery(id+"F0.wireOp",EDGE,"E85")}),-1.0]])]});
            var Q26;
            Q26=makeQuery(id+"F0.imprint","IMPRINT",FACE,{"disambiguationData":[TD([[makeQuery(id+"F0.imprint","IMPRINT",EDGE,{"derivedFrom":sQuery(id+"F0.wireOp",EDGE,"E98")}),-1.0]])]});
            var Q27;
            {var subQ0=sQuery(id+"F0.wireOp",EDGE,"E53");var subQ1=sQuery(id+"F0.wireOp",EDGE,"E36");var subQ2=makeQuery(id+"F0.imprint","INTERSECT",VERTEX,{"derivedFrom":[subQ1,subQ0]});Q27=makeQuery(id+"F0.imprint","IMPRINT",FACE,{"disambiguationData":[TD([[makeQuery(id+"F0.imprint","IMPRINT",EDGE,{"disambiguationData":[TD([[subQ2,1.0]])],"derivedFrom":subQ1}),-1.0]])]});}
            var Q28;
            {var subQ0=sQuery(id+"F0.wireOp",EDGE,"E12");Q28=makeQuery(id+"F0.imprint","IMPRINT",FACE,{"disambiguationData":[TD([[makeQuery(id+"F0.imprint","IMPRINT",EDGE,{"derivedFrom":subQ0}),-1.0]])]});}
            var Q29;
            {var subQ3=sQuery(id+"F0.wireOp",EDGE,"E8");var subQ5=sQuery(id+"F0.wireOp",EDGE,"E233");var subQ6=makeQuery(id+"F0.imprint","INTERSECT",VERTEX,{"derivedFrom":[subQ3,subQ5]});Q29=makeQuery(id+"F0.imprint","IMPRINT",FACE,{"disambiguationData":[TD([[makeQuery(id+"F0.imprint","IMPRINT",EDGE,{"disambiguationData":[TD([[subQ6,-1.0]])],"derivedFrom":subQ3}),1.0]])]});}
            var Q30;
            Q30=makeQuery(id+"F0.imprint","IMPRINT",FACE,{"disambiguationData":[TD([[makeQuery(id+"F0.imprint","IMPRINT",EDGE,{"derivedFrom":sQuery(id+"F0.wireOp",EDGE,"E165")}),1.0]])]});
            var Q31;
            Q31=makeQuery(id+"F0.imprint","IMPRINT",FACE,{"disambiguationData":[TD([[makeQuery(id+"F0.imprint","IMPRINT",EDGE,{"derivedFrom":sQuery(id+"F0.wireOp",EDGE,"E190")}),-1.0]])]});
            var Q32;
            {var subQ1=sQuery(id+"F0.wireOp",EDGE,"E13");Q32=makeQuery(id+"F0.imprint","IMPRINT",FACE,{"disambiguationData":[TD([[makeQuery(id+"F0.imprint","IMPRINT",EDGE,{"derivedFrom":subQ1}),1.0]])]});}
            var Q33;
            {var subQ0=sQuery(id+"F0.wireOp",EDGE,"E15");var subQ1=sQuery(id+"F0.wireOp",EDGE,"E14");var subQ2=makeQuery(id+"F0.imprint","INTERSECT",VERTEX,{"derivedFrom":[subQ1,subQ0]});Q33=makeQuery(id+"F0.imprint","IMPRINT",FACE,{"disambiguationData":[TD([[makeQuery(id+"F0.imprint","IMPRINT",EDGE,{"disambiguationData":[TD([[subQ2,1.0]])],"derivedFrom":subQ1}),1.0]])]});}
            var Q34;
            {var subQ0=sQuery(id+"F0.wireOp",EDGE,"E7");Q34=makeQuery(id+"F0.imprint","IMPRINT",FACE,{"disambiguationData":[TD([[makeQuery(id+"F0.imprint","IMPRINT",EDGE,{"derivedFrom":subQ0}),-1.0]])]});}
            var Q35;
            {var subQ0=sQuery(id+"F0.wireOp",EDGE,"E200");var subQ1=sQuery(id+"F0.wireOp",EDGE,"E193");var subQ2=makeQuery(id+"F0.imprint","INTERSECT",VERTEX,{"derivedFrom":[subQ1,subQ0]});Q35=makeQuery(id+"F0.imprint","IMPRINT",FACE,{"disambiguationData":[TD([[makeQuery(id+"F0.imprint","IMPRINT",EDGE,{"disambiguationData":[TD([[subQ2,1.0]])],"derivedFrom":subQ1}),-1.0]])]});}
            var Q36;
            {var subQ0=sQuery(id+"F0.wireOp",EDGE,"E129");var subQ1=sQuery(id+"F0.wireOp",EDGE,"E128");var subQ2=makeQuery(id+"F0.imprint","INTERSECT",VERTEX,{"derivedFrom":[subQ1,subQ0]});Q36=makeQuery(id+"F0.imprint","IMPRINT",FACE,{"disambiguationData":[TD([[makeQuery(id+"F0.imprint","IMPRINT",EDGE,{"disambiguationData":[TD([[subQ2,1.0]])],"derivedFrom":subQ1}),-1.0]])]});}
            var Q37;
            Q37=makeQuery(id+"F0.imprint","IMPRINT",FACE,{"disambiguationData":[TD([[makeQuery(id+"F0.imprint","IMPRINT",EDGE,{"derivedFrom":sQuery(id+"F0.wireOp",EDGE,"E165")}),-1.0]])]});
            var Q38;
            {var subQ0=sQuery(id+"F0.wireOp",EDGE,"E10");Q38=makeQuery(id+"F0.imprint","IMPRINT",FACE,{"disambiguationData":[TD([[makeQuery(id+"F0.imprint","IMPRINT",EDGE,{"derivedFrom":subQ0}),1.0]])]});}
            var Q39;
            Q39=makeQuery(id+"F0.imprint","IMPRINT",FACE,{"disambiguationData":[TD([[makeQuery(id+"F0.imprint","IMPRINT",EDGE,{"derivedFrom":sQuery(id+"F0.wireOp",EDGE,"E23")}),1.0]])]});
            var Q40;
            Q40=makeQuery(id+"F0.imprint","IMPRINT",FACE,{"disambiguationData":[TD([[makeQuery(id+"F0.imprint","IMPRINT",EDGE,{"derivedFrom":sQuery(id+"F0.wireOp",EDGE,"E33")}),1.0]])]});
            var Q41;
            {var subQ0=sQuery(id+"F0.wireOp",EDGE,"E240");var subQ1=sQuery(id+"F0.wireOp",EDGE,"E8");var subQ2=makeQuery(id+"F0.imprint","INTERSECT",VERTEX,{"derivedFrom":[subQ1,subQ0]});Q41=makeQuery(id+"F0.imprint","IMPRINT",FACE,{"disambiguationData":[TD([[makeQuery(id+"F0.imprint","IMPRINT",EDGE,{"disambiguationData":[TD([[subQ2,-1.0]])],"derivedFrom":subQ1}),-1.0]])]});}
            var Q42;
            {var subQ5=sQuery(id+"F0.wireOp",EDGE,"E120");Q42=makeQuery(id+"F0.imprint","IMPRINT",FACE,{"disambiguationData":[TD([[makeQuery(id+"F0.imprint","IMPRINT",EDGE,{"derivedFrom":subQ5}),1.0]])]});}
            var Q43;
            {var subQ0=sQuery(id+"F0.wireOp",EDGE,"E232");var subQ1=sQuery(id+"F0.wireOp",EDGE,"E8");var subQ2=makeQuery(id+"F0.imprint","INTERSECT",VERTEX,{"derivedFrom":[subQ1,subQ0]});Q43=makeQuery(id+"F0.imprint","IMPRINT",FACE,{"disambiguationData":[TD([[makeQuery(id+"F0.imprint","IMPRINT",EDGE,{"disambiguationData":[TD([[subQ2,-1.0]])],"derivedFrom":subQ1}),-1.0]])]});}
            var Q44;
            {var subQ5=sQuery(id+"F0.wireOp",EDGE,"E188");var subQ6=sQuery(id+"F0.wireOp",EDGE,"E178");var subQ7=makeQuery(id+"F0.imprint","INTERSECT",VERTEX,{"derivedFrom":[subQ6,subQ5]});Q44=makeQuery(id+"F0.imprint","IMPRINT",FACE,{"disambiguationData":[TD([[makeQuery(id+"F0.imprint","IMPRINT",EDGE,{"disambiguationData":[TD([[subQ7,1.0]])],"derivedFrom":subQ6}),1.0]])]});}
            var Q45;
            Q45=makeQuery(id+"F0.imprint","IMPRINT",FACE,{"disambiguationData":[TD([[makeQuery(id+"F0.imprint","IMPRINT",EDGE,{"derivedFrom":sQuery(id+"F0.wireOp",EDGE,"E192")}),-1.0]])]});
            var Q46;
            {var subQ0=sQuery(id+"F0.wireOp",EDGE,"E21");Q46=makeQuery(id+"F0.imprint","IMPRINT",FACE,{"disambiguationData":[TD([[makeQuery(id+"F0.imprint","IMPRINT",EDGE,{"derivedFrom":subQ0}),-1.0]])]});}
            var Q47;
            Q47=makeQuery(id+"F0.imprint","IMPRINT",FACE,{"disambiguationData":[TD([[makeQuery(id+"F0.imprint","IMPRINT",EDGE,{"derivedFrom":sQuery(id+"F0.wireOp",EDGE,"E206")}),-1.0]])]});
            var Q48;
            {var subQ1=sQuery(id+"F0.wireOp",EDGE,"E220");Q48=makeQuery(id+"F0.imprint","IMPRINT",FACE,{"disambiguationData":[TD([[makeQuery(id+"F0.imprint","IMPRINT",EDGE,{"derivedFrom":subQ1}),1.0]])]});}
            var Q49;
            {var subQ1=sQuery(id+"F0.wireOp",EDGE,"E16");Q49=makeQuery(id+"F0.imprint","IMPRINT",FACE,{"disambiguationData":[TD([[makeQuery(id+"F0.imprint","IMPRINT",EDGE,{"derivedFrom":subQ1}),-1.0]])]});}
            var Q50;
            Q50=makeQuery(id+"F0.imprint","IMPRINT",FACE,{"disambiguationData":[TD([[makeQuery(id+"F0.imprint","IMPRINT",EDGE,{"derivedFrom":sQuery(id+"F0.wireOp",EDGE,"E67")}),1.0]])]});
            var Q51;
            Q51=makeQuery(id+"F0.imprint","IMPRINT",FACE,{"disambiguationData":[TD([[makeQuery(id+"F0.imprint","IMPRINT",EDGE,{"derivedFrom":sQuery(id+"F0.wireOp",EDGE,"E164")}),-1.0]])]});
            var Q52;
            Q52=makeQuery(id+"F0.imprint","IMPRINT",FACE,{"disambiguationData":[TD([[makeQuery(id+"F0.imprint","IMPRINT",EDGE,{"derivedFrom":sQuery(id+"F0.wireOp",EDGE,"E144")}),-1.0]])]});
            var Q53;
            {var subQ0=sQuery(id+"F0.wireOp",EDGE,"E223");var subQ1=sQuery(id+"F0.wireOp",EDGE,"E8");var subQ2=makeQuery(id+"F0.imprint","INTERSECT",VERTEX,{"derivedFrom":[subQ1,subQ0]});Q53=makeQuery(id+"F0.imprint","IMPRINT",FACE,{"disambiguationData":[TD([[makeQuery(id+"F0.imprint","IMPRINT",EDGE,{"disambiguationData":[TD([[subQ2,-1.0]])],"derivedFrom":subQ1}),1.0]])]});}
            var Q54;
            Q54=makeQuery(id+"F0.imprint","IMPRINT",FACE,{"disambiguationData":[TD([[makeQuery(id+"F0.imprint","IMPRINT",EDGE,{"derivedFrom":sQuery(id+"F0.wireOp",EDGE,"E67")}),-1.0]])]});
            var Q55;
            {var subQ4=sQuery(id+"F0.wireOp",EDGE,"E225");Q55=makeQuery(id+"F0.imprint","IMPRINT",FACE,{"disambiguationData":[TD([[makeQuery(id+"F0.imprint","IMPRINT",EDGE,{"derivedFrom":subQ4}),-1.0]])]});}
            var Q56;
            Q56=makeQuery(id+"F0.imprint","IMPRINT",FACE,{"disambiguationData":[TD([[makeQuery(id+"F0.imprint","IMPRINT",EDGE,{"derivedFrom":sQuery(id+"F0.wireOp",EDGE,"E134")}),-1.0]])]});
            var Q57;
            Q57=makeQuery(id+"F0.imprint","IMPRINT",FACE,{"disambiguationData":[TD([[makeQuery(id+"F0.imprint","IMPRINT",EDGE,{"derivedFrom":sQuery(id+"F0.wireOp",EDGE,"E118")}),1.0]])]});
            var Q58;
            {var subQ0=sQuery(id+"F0.wireOp",EDGE,"E236");var subQ1=sQuery(id+"F0.wireOp",EDGE,"E8");var subQ2=makeQuery(id+"F0.imprint","INTERSECT",VERTEX,{"derivedFrom":[subQ1,subQ0]});Q58=makeQuery(id+"F0.imprint","IMPRINT",FACE,{"disambiguationData":[TD([[makeQuery(id+"F0.imprint","IMPRINT",EDGE,{"disambiguationData":[TD([[subQ2,1.0]])],"derivedFrom":subQ1}),-1.0]])]});}
            var Q59;
            {var subQ0=sQuery(id+"F0.wireOp",EDGE,"E1");Q59=makeQuery(id+"F0.imprint","IMPRINT",FACE,{"disambiguationData":[TD([[makeQuery(id+"F0.imprint","IMPRINT",EDGE,{"derivedFrom":subQ0}),-1.0]])]});}
            var Q60;
            {var subQ0=sQuery(id+"F0.wireOp",EDGE,"E82");Q60=makeQuery(id+"F0.imprint","IMPRINT",FACE,{"disambiguationData":[TD([[makeQuery(id+"F0.imprint","IMPRINT",EDGE,{"derivedFrom":subQ0}),-1.0]])]});}
            var Q61;
            {var subQ0=sQuery(id+"F0.wireOp",EDGE,"E93");Q61=makeQuery(id+"F0.imprint","IMPRINT",FACE,{"disambiguationData":[TD([[makeQuery(id+"F0.imprint","IMPRINT",EDGE,{"derivedFrom":subQ0}),1.0]])]});}
            var Q62;
            {var subQ0=sQuery(id+"F0.wireOp",EDGE,"E233");var subQ1=sQuery(id+"F0.wireOp",EDGE,"E232");var subQ2=makeQuery(id+"F0.imprint","INTERSECT",VERTEX,{"derivedFrom":[subQ1,subQ0]});Q62=makeQuery(id+"F0.imprint","IMPRINT",FACE,{"disambiguationData":[TD([[makeQuery(id+"F0.imprint","IMPRINT",EDGE,{"disambiguationData":[TD([[subQ2,1.0]])],"derivedFrom":subQ1}),-1.0]])]});}
            var Q63;
            {var subQ0=sQuery(id+"F0.wireOp",EDGE,"E198");var subQ1=sQuery(id+"F0.wireOp",EDGE,"E191");var subQ2=makeQuery(id+"F0.imprint","INTERSECT",VERTEX,{"derivedFrom":[subQ1,subQ0]});Q63=makeQuery(id+"F0.imprint","IMPRINT",FACE,{"disambiguationData":[TD([[makeQuery(id+"F0.imprint","IMPRINT",EDGE,{"disambiguationData":[TD([[subQ2,-1.0]])],"derivedFrom":subQ1}),1.0]])]});}
            var Q64;
            {var subQ0=sQuery(id+"F0.wireOp",EDGE,"E199");Q64=makeQuery(id+"F0.imprint","IMPRINT",FACE,{"disambiguationData":[TD([[makeQuery(id+"F0.imprint","IMPRINT",EDGE,{"derivedFrom":subQ0}),-1.0]])]});}
            var Q65;
            {var subQ0=sQuery(id+"F0.wireOp",EDGE,"E3");Q65=makeQuery(id+"F0.imprint","IMPRINT",FACE,{"disambiguationData":[TD([[makeQuery(id+"F0.imprint","IMPRINT",EDGE,{"derivedFrom":subQ0}),-1.0]])]});}
            var Q66;
            {var subQ0=sQuery(id+"F0.wireOp",EDGE,"E231");var subQ1=sQuery(id+"F0.wireOp",EDGE,"E194");var subQ2=makeQuery(id+"F0.imprint","INTERSECT",VERTEX,{"derivedFrom":[subQ1,subQ0]});Q66=makeQuery(id+"F0.imprint","IMPRINT",FACE,{"disambiguationData":[TD([[makeQuery(id+"F0.imprint","IMPRINT",EDGE,{"disambiguationData":[TD([[subQ2,-1.0]])],"derivedFrom":subQ1}),1.0]])]});}
            var Q67;
            {var subQ0=sQuery(id+"F0.wireOp",EDGE,"E203");var subQ1=sQuery(id+"F0.wireOp",EDGE,"E195");var subQ2=makeQuery(id+"F0.imprint","INTERSECT",VERTEX,{"derivedFrom":[subQ1,subQ0]});Q67=makeQuery(id+"F0.imprint","IMPRINT",FACE,{"disambiguationData":[TD([[makeQuery(id+"F0.imprint","IMPRINT",EDGE,{"disambiguationData":[TD([[subQ2,1.0]])],"derivedFrom":subQ1}),-1.0]])]});}
            var Q68;
            {var subQ0=sQuery(id+"F0.wireOp",EDGE,"E74");var subQ1=sQuery(id+"F0.wireOp",EDGE,"E72");var subQ2=makeQuery(id+"F0.imprint","INTERSECT",VERTEX,{"derivedFrom":[subQ1,subQ0]});Q68=makeQuery(id+"F0.imprint","IMPRINT",FACE,{"disambiguationData":[TD([[makeQuery(id+"F0.imprint","IMPRINT",EDGE,{"disambiguationData":[TD([[subQ2,1.0]])],"derivedFrom":subQ1}),-1.0]])]});}
            var Q69;
            {var subQ0=sQuery(id+"F0.wireOp",EDGE,"E175");Q69=makeQuery(id+"F0.imprint","IMPRINT",FACE,{"disambiguationData":[TD([[makeQuery(id+"F0.imprint","IMPRINT",EDGE,{"derivedFrom":subQ0}),1.0]])]});}
            var Q70;
            {var subQ0=sQuery(id+"F0.wireOp",EDGE,"E163");var subQ1=sQuery(id+"F0.wireOp",EDGE,"E155");var subQ2=makeQuery(id+"F0.imprint","INTERSECT",VERTEX,{"derivedFrom":[subQ1,subQ0]});Q70=makeQuery(id+"F0.imprint","IMPRINT",FACE,{"disambiguationData":[TD([[makeQuery(id+"F0.imprint","IMPRINT",EDGE,{"disambiguationData":[TD([[subQ2,1.0]])],"derivedFrom":subQ1}),1.0]])]});}
            var Q71;
            {var subQ0=sQuery(id+"F0.wireOp",EDGE,"E77");var subQ1=sQuery(id+"F0.wireOp",EDGE,"E62");var subQ2=makeQuery(id+"F0.imprint","INTERSECT",VERTEX,{"derivedFrom":[subQ1,subQ0]});Q71=makeQuery(id+"F0.imprint","IMPRINT",FACE,{"disambiguationData":[TD([[makeQuery(id+"F0.imprint","IMPRINT",EDGE,{"disambiguationData":[TD([[subQ2,1.0]])],"derivedFrom":subQ1}),1.0]])]});}
            var Q72;
            {var subQ0=sQuery(id+"F0.wireOp",EDGE,"E182");var subQ1=sQuery(id+"F0.wireOp",EDGE,"E172");var subQ2=makeQuery(id+"F0.imprint","INTERSECT",VERTEX,{"derivedFrom":[subQ1,subQ0]});Q72=makeQuery(id+"F0.imprint","IMPRINT",FACE,{"disambiguationData":[TD([[makeQuery(id+"F0.imprint","IMPRINT",EDGE,{"disambiguationData":[TD([[subQ2,-1.0]])],"derivedFrom":subQ1}),-1.0]])]});}
            extrude(context, id + "F1", {"entities" : qUnion([Q0, Q1, Q2, Q3, Q4, Q5, Q6, Q7, Q8, Q9, Q10, Q11, Q12, Q13, Q14, Q15, Q16, Q17, Q18, Q19, Q20, Q21, Q22, Q23, Q24, Q25, Q26, Q27, Q28, Q29, Q30, Q31, Q32, Q33, Q34, Q35, Q36, Q37, Q38, Q39, Q40, Q41, Q42, Q43, Q44, Q45, Q46, Q47, Q48, Q49, Q50, Q51, Q52, Q53, Q54, Q55, Q56, Q57, Q58, Q59, Q60, Q61, Q62, Q63, Q64, Q65, Q66, Q67, Q68, Q69, Q70, Q71, Q72]), "oppositeDirection" : true, "depth" : 4.8 * mm, "offsetDistance" : 25.4 * mm});
        }
        {
            var Q0;
            {var subQ0=sQuery(id+"F0.wireOp",EDGE,"E12");Q0=makeQuery(id+"F0.imprint","IMPRINT",FACE,{"disambiguationData":[TD([[makeQuery(id+"F0.imprint","IMPRINT",EDGE,{"derivedFrom":subQ0}),-1.0]])]});}
            var Q1;
            Q1=makeQuery(id+"F0.imprint","IMPRINT",FACE,{"disambiguationData":[TD([[makeQuery(id+"F0.imprint","IMPRINT",EDGE,{"derivedFrom":sQuery(id+"F0.wireOp",EDGE,"E33")}),1.0]])]});
            var Q2;
            {var subQ0=sQuery(id+"F0.wireOp",EDGE,"E53");var subQ1=sQuery(id+"F0.wireOp",EDGE,"E36");var subQ2=makeQuery(id+"F0.imprint","INTERSECT",VERTEX,{"derivedFrom":[subQ1,subQ0]});Q2=makeQuery(id+"F0.imprint","IMPRINT",FACE,{"disambiguationData":[TD([[makeQuery(id+"F0.imprint","IMPRINT",EDGE,{"disambiguationData":[TD([[subQ2,1.0]])],"derivedFrom":subQ1}),-1.0]])]});}
            var Q3;
            Q3=makeQuery(id+"F0.imprint","IMPRINT",FACE,{"disambiguationData":[TD([[makeQuery(id+"F0.imprint","IMPRINT",EDGE,{"derivedFrom":sQuery(id+"F0.wireOp",EDGE,"E67")}),-1.0]])]});
            var Q4;
            Q4=makeQuery(id+"F0.imprint","IMPRINT",FACE,{"disambiguationData":[TD([[makeQuery(id+"F0.imprint","IMPRINT",EDGE,{"derivedFrom":sQuery(id+"F0.wireOp",EDGE,"E81")}),1.0]])]});
            var Q5;
            Q5=makeQuery(id+"F0.imprint","IMPRINT",FACE,{"disambiguationData":[TD([[makeQuery(id+"F0.imprint","IMPRINT",EDGE,{"derivedFrom":sQuery(id+"F0.wireOp",EDGE,"E85")}),-1.0]])]});
            var Q6;
            {var subQ0=sQuery(id+"F0.wireOp",EDGE,"E93");Q6=makeQuery(id+"F0.imprint","IMPRINT",FACE,{"disambiguationData":[TD([[makeQuery(id+"F0.imprint","IMPRINT",EDGE,{"derivedFrom":subQ0}),1.0]])]});}
            var Q7;
            {var subQ0=sQuery(id+"F0.wireOp",EDGE,"E82");Q7=makeQuery(id+"F0.imprint","IMPRINT",FACE,{"disambiguationData":[TD([[makeQuery(id+"F0.imprint","IMPRINT",EDGE,{"derivedFrom":subQ0}),-1.0]])]});}
            var Q8;
            Q8=makeQuery(id+"F0.imprint","IMPRINT",FACE,{"disambiguationData":[TD([[makeQuery(id+"F0.imprint","IMPRINT",EDGE,{"derivedFrom":sQuery(id+"F0.wireOp",EDGE,"E98")}),-1.0]])]});
            var Q9;
            Q9=makeQuery(id+"F0.imprint","IMPRINT",FACE,{"disambiguationData":[TD([[makeQuery(id+"F0.imprint","IMPRINT",EDGE,{"derivedFrom":sQuery(id+"F0.wireOp",EDGE,"E118")}),1.0]])]});
            var Q10;
            Q10=makeQuery(id+"F0.imprint","IMPRINT",FACE,{"disambiguationData":[TD([[makeQuery(id+"F0.imprint","IMPRINT",EDGE,{"derivedFrom":sQuery(id+"F0.wireOp",EDGE,"E206")}),-1.0]])]});
            var Q11;
            {var subQ0=sQuery(id+"F0.wireOp",EDGE,"E199");Q11=makeQuery(id+"F0.imprint","IMPRINT",FACE,{"disambiguationData":[TD([[makeQuery(id+"F0.imprint","IMPRINT",EDGE,{"derivedFrom":subQ0}),-1.0]])]});}
            var Q12;
            Q12=makeQuery(id+"F0.imprint","IMPRINT",FACE,{"disambiguationData":[TD([[makeQuery(id+"F0.imprint","IMPRINT",EDGE,{"derivedFrom":sQuery(id+"F0.wireOp",EDGE,"E190")}),-1.0]])]});
            var Q13;
            {var subQ0=sQuery(id+"F0.wireOp",EDGE,"E200");var subQ1=sQuery(id+"F0.wireOp",EDGE,"E193");var subQ2=makeQuery(id+"F0.imprint","INTERSECT",VERTEX,{"derivedFrom":[subQ1,subQ0]});Q13=makeQuery(id+"F0.imprint","IMPRINT",FACE,{"disambiguationData":[TD([[makeQuery(id+"F0.imprint","IMPRINT",EDGE,{"disambiguationData":[TD([[subQ2,1.0]])],"derivedFrom":subQ1}),-1.0]])]});}
            var Q14;
            Q14=makeQuery(id+"F0.imprint","IMPRINT",FACE,{"disambiguationData":[TD([[makeQuery(id+"F0.imprint","IMPRINT",EDGE,{"derivedFrom":sQuery(id+"F0.wireOp",EDGE,"E192")}),-1.0]])]});
            var Q15;
            Q15=makeQuery(id+"F0.imprint","IMPRINT",FACE,{"disambiguationData":[TD([[makeQuery(id+"F0.imprint","IMPRINT",EDGE,{"derivedFrom":sQuery(id+"F0.wireOp",EDGE,"E173")}),-1.0]])]});
            var Q16;
            {var subQ5=sQuery(id+"F0.wireOp",EDGE,"E188");var subQ6=sQuery(id+"F0.wireOp",EDGE,"E178");var subQ7=makeQuery(id+"F0.imprint","INTERSECT",VERTEX,{"derivedFrom":[subQ6,subQ5]});Q16=makeQuery(id+"F0.imprint","IMPRINT",FACE,{"disambiguationData":[TD([[makeQuery(id+"F0.imprint","IMPRINT",EDGE,{"disambiguationData":[TD([[subQ7,1.0]])],"derivedFrom":subQ6}),1.0]])]});}
            var Q17;
            {var subQ0=sQuery(id+"F0.wireOp",EDGE,"E175");Q17=makeQuery(id+"F0.imprint","IMPRINT",FACE,{"disambiguationData":[TD([[makeQuery(id+"F0.imprint","IMPRINT",EDGE,{"derivedFrom":subQ0}),1.0]])]});}
            var Q18;
            Q18=makeQuery(id+"F0.imprint","IMPRINT",FACE,{"disambiguationData":[TD([[makeQuery(id+"F0.imprint","IMPRINT",EDGE,{"derivedFrom":sQuery(id+"F0.wireOp",EDGE,"E165")}),1.0]])]});
            var Q19;
            Q19=makeQuery(id+"F0.imprint","IMPRINT",FACE,{"disambiguationData":[TD([[makeQuery(id+"F0.imprint","IMPRINT",EDGE,{"derivedFrom":sQuery(id+"F0.wireOp",EDGE,"E164")}),-1.0]])]});
            var Q20;
            Q20=makeQuery(id+"F0.imprint","IMPRINT",FACE,{"disambiguationData":[TD([[makeQuery(id+"F0.imprint","IMPRINT",EDGE,{"derivedFrom":sQuery(id+"F0.wireOp",EDGE,"E144")}),-1.0]])]});
            var Q21;
            Q21=makeQuery(id+"F0.imprint","IMPRINT",FACE,{"disambiguationData":[TD([[makeQuery(id+"F0.imprint","IMPRINT",EDGE,{"derivedFrom":sQuery(id+"F0.wireOp",EDGE,"E134")}),-1.0]])]});
            var Q22;
            Q22=makeQuery(id+"F0.imprint","IMPRINT",FACE,{"disambiguationData":[TD([[makeQuery(id+"F0.imprint","IMPRINT",EDGE,{"derivedFrom":sQuery(id+"F0.wireOp",EDGE,"E23")}),1.0]])]});
            var Q23;
            {var subQ0=sQuery(id+"F0.wireOp",EDGE,"E21");Q23=makeQuery(id+"F0.imprint","IMPRINT",FACE,{"disambiguationData":[TD([[makeQuery(id+"F0.imprint","IMPRINT",EDGE,{"derivedFrom":subQ0}),-1.0]])]});}
            var Q24;
            {var subQ1=sQuery(id+"F0.wireOp",EDGE,"E16");Q24=makeQuery(id+"F0.imprint","IMPRINT",FACE,{"disambiguationData":[TD([[makeQuery(id+"F0.imprint","IMPRINT",EDGE,{"derivedFrom":subQ1}),-1.0]])]});}
            var Q25;
            {var subQ1=sQuery(id+"F0.wireOp",EDGE,"E13");Q25=makeQuery(id+"F0.imprint","IMPRINT",FACE,{"disambiguationData":[TD([[makeQuery(id+"F0.imprint","IMPRINT",EDGE,{"derivedFrom":subQ1}),1.0]])]});}
            var Q26;
            {var subQ5=sQuery(id+"F0.wireOp",EDGE,"E120");Q26=makeQuery(id+"F0.imprint","IMPRINT",FACE,{"disambiguationData":[TD([[makeQuery(id+"F0.imprint","IMPRINT",EDGE,{"derivedFrom":subQ5}),1.0]])]});}
            extrude(context, id + "F2", {"entities" : qUnion([Q0, Q1, Q2, Q3, Q4, Q5, Q6, Q7, Q8, Q9, Q10, Q11, Q12, Q13, Q14, Q15, Q16, Q17, Q18, Q19, Q20, Q21, Q22, Q23, Q24, Q25, Q26]), "operationType" : NewBodyOperationType.ADD, "depth" : 11.2 * mm, "offsetDistance" : 25.4 * mm});
        }
        {
            var Q0;
            {var subQ0=sQuery(id+"F0.wireOp",EDGE,"E182");var subQ1=sQuery(id+"F0.wireOp",EDGE,"E172");var subQ2=makeQuery(id+"F0.imprint","INTERSECT",VERTEX,{"derivedFrom":[subQ1,subQ0]});Q0=makeQuery(id+"F0.imprint","IMPRINT",FACE,{"disambiguationData":[TD([[makeQuery(id+"F0.imprint","IMPRINT",EDGE,{"disambiguationData":[TD([[subQ2,-1.0]])],"derivedFrom":subQ1}),-1.0]])]});}
            var Q1;
            {var subQ0=sQuery(id+"F0.wireOp",EDGE,"E231");var subQ1=sQuery(id+"F0.wireOp",EDGE,"E194");var subQ2=makeQuery(id+"F0.imprint","INTERSECT",VERTEX,{"derivedFrom":[subQ1,subQ0]});Q1=makeQuery(id+"F0.imprint","IMPRINT",FACE,{"disambiguationData":[TD([[makeQuery(id+"F0.imprint","IMPRINT",EDGE,{"disambiguationData":[TD([[subQ2,-1.0]])],"derivedFrom":subQ1}),1.0]])]});}
            var Q2;
            {var subQ0=sQuery(id+"F0.wireOp",EDGE,"E203");var subQ1=sQuery(id+"F0.wireOp",EDGE,"E195");var subQ2=makeQuery(id+"F0.imprint","INTERSECT",VERTEX,{"derivedFrom":[subQ1,subQ0]});Q2=makeQuery(id+"F0.imprint","IMPRINT",FACE,{"disambiguationData":[TD([[makeQuery(id+"F0.imprint","IMPRINT",EDGE,{"disambiguationData":[TD([[subQ2,1.0]])],"derivedFrom":subQ1}),-1.0]])]});}
            var Q3;
            {var subQ0=sQuery(id+"F0.wireOp",EDGE,"E77");var subQ1=sQuery(id+"F0.wireOp",EDGE,"E62");var subQ2=makeQuery(id+"F0.imprint","INTERSECT",VERTEX,{"derivedFrom":[subQ1,subQ0]});Q3=makeQuery(id+"F0.imprint","IMPRINT",FACE,{"disambiguationData":[TD([[makeQuery(id+"F0.imprint","IMPRINT",EDGE,{"disambiguationData":[TD([[subQ2,1.0]])],"derivedFrom":subQ1}),1.0]])]});}
            var Q4;
            {var subQ0=sQuery(id+"F0.wireOp",EDGE,"E163");var subQ1=sQuery(id+"F0.wireOp",EDGE,"E155");var subQ2=makeQuery(id+"F0.imprint","INTERSECT",VERTEX,{"derivedFrom":[subQ1,subQ0]});Q4=makeQuery(id+"F0.imprint","IMPRINT",FACE,{"disambiguationData":[TD([[makeQuery(id+"F0.imprint","IMPRINT",EDGE,{"disambiguationData":[TD([[subQ2,1.0]])],"derivedFrom":subQ1}),1.0]])]});}
            var Q5;
            Q5=makeQuery(id+"F0.imprint","IMPRINT",FACE,{"disambiguationData":[TD([[makeQuery(id+"F0.imprint","IMPRINT",EDGE,{"derivedFrom":sQuery(id+"F0.wireOp",EDGE,"E165")}),1.0]])]});
            var Q6;
            {var subQ0=sQuery(id+"F0.wireOp",EDGE,"E198");var subQ1=sQuery(id+"F0.wireOp",EDGE,"E191");var subQ2=makeQuery(id+"F0.imprint","INTERSECT",VERTEX,{"derivedFrom":[subQ1,subQ0]});Q6=makeQuery(id+"F0.imprint","IMPRINT",FACE,{"disambiguationData":[TD([[makeQuery(id+"F0.imprint","IMPRINT",EDGE,{"disambiguationData":[TD([[subQ2,-1.0]])],"derivedFrom":subQ1}),1.0]])]});}
            var Q7;
            {var subQ10=sQuery(id+"F0.wireOp",EDGE,"E224");Q7=makeQuery(id+"F0.imprint","IMPRINT",FACE,{"disambiguationData":[TD([[makeQuery(id+"F0.imprint","IMPRINT",EDGE,{"derivedFrom":subQ10}),1.0]])]});}
            var Q8;
            {var subQ6=sQuery(id+"F0.wireOp",EDGE,"E93");Q8=makeQuery(id+"F0.imprint","IMPRINT",FACE,{"disambiguationData":[TD([[makeQuery(id+"F0.imprint","IMPRINT",EDGE,{"derivedFrom":subQ6}),-1.0]])]});}
            var Q9;
            {var subQ0=sQuery(id+"F0.wireOp",EDGE,"E223");var subQ1=sQuery(id+"F0.wireOp",EDGE,"E8");var subQ2=makeQuery(id+"F0.imprint","INTERSECT",VERTEX,{"derivedFrom":[subQ1,subQ0]});Q9=makeQuery(id+"F0.imprint","IMPRINT",FACE,{"disambiguationData":[TD([[makeQuery(id+"F0.imprint","IMPRINT",EDGE,{"disambiguationData":[TD([[subQ2,-1.0]])],"derivedFrom":subQ1}),-1.0]])]});}
            var Q10;
            {var subQ0=sQuery(id+"F0.wireOp",EDGE,"E228");var subQ1=sQuery(id+"F0.wireOp",EDGE,"E8");var subQ2=makeQuery(id+"F0.imprint","INTERSECT",VERTEX,{"derivedFrom":[subQ1,subQ0]});Q10=makeQuery(id+"F0.imprint","IMPRINT",FACE,{"disambiguationData":[TD([[makeQuery(id+"F0.imprint","IMPRINT",EDGE,{"disambiguationData":[TD([[subQ2,1.0]])],"derivedFrom":subQ1}),-1.0]])]});}
            var Q11;
            Q11=makeQuery(id+"F0.imprint","IMPRINT",FACE,{"disambiguationData":[TD([[makeQuery(id+"F0.imprint","IMPRINT",EDGE,{"derivedFrom":sQuery(id+"F0.wireOp",EDGE,"E173")}),-1.0]])]});
            var Q12;
            {var subQ0=sQuery(id+"F0.wireOp",EDGE,"E200");var subQ1=sQuery(id+"F0.wireOp",EDGE,"E193");var subQ2=makeQuery(id+"F0.imprint","INTERSECT",VERTEX,{"derivedFrom":[subQ1,subQ0]});Q12=makeQuery(id+"F0.imprint","IMPRINT",FACE,{"disambiguationData":[TD([[makeQuery(id+"F0.imprint","IMPRINT",EDGE,{"disambiguationData":[TD([[subQ2,1.0]])],"derivedFrom":subQ1}),-1.0]])]});}
            var Q13;
            Q13=makeQuery(id+"F0.imprint","IMPRINT",FACE,{"disambiguationData":[TD([[makeQuery(id+"F0.imprint","IMPRINT",EDGE,{"derivedFrom":sQuery(id+"F0.wireOp",EDGE,"E165")}),-1.0]])]});
            var Q14;
            Q14=makeQuery(id+"F0.imprint","IMPRINT",FACE,{"disambiguationData":[TD([[makeQuery(id+"F0.imprint","IMPRINT",EDGE,{"derivedFrom":sQuery(id+"F0.wireOp",EDGE,"E67")}),1.0]])]});
            var Q15;
            {var subQ0=sQuery(id+"F0.wireOp",EDGE,"E225");Q15=makeQuery(id+"F0.imprint","IMPRINT",FACE,{"disambiguationData":[TD([[makeQuery(id+"F0.imprint","IMPRINT",EDGE,{"derivedFrom":subQ0}),-1.0]])]});}
            var Q16;
            {var subQ0=sQuery(id+"F0.wireOp",EDGE,"E177");Q16=makeQuery(id+"F0.imprint","IMPRINT",FACE,{"disambiguationData":[TD([[makeQuery(id+"F0.imprint","IMPRINT",EDGE,{"derivedFrom":subQ0}),-1.0]])]});}
            var Q17;
            Q17=makeQuery(id+"F0.imprint","IMPRINT",FACE,{"disambiguationData":[TD([[makeQuery(id+"F0.imprint","IMPRINT",EDGE,{"derivedFrom":sQuery(id+"F0.wireOp",EDGE,"E67")}),-1.0]])]});
            var Q18;
            Q18=makeQuery(id+"F0.imprint","IMPRINT",FACE,{"disambiguationData":[TD([[makeQuery(id+"F0.imprint","IMPRINT",EDGE,{"derivedFrom":sQuery(id+"F0.wireOp",EDGE,"E81")}),1.0]])]});
            var Q19;
            {var subQ0=sQuery(id+"F0.wireOp",EDGE,"E74");var subQ1=sQuery(id+"F0.wireOp",EDGE,"E72");var subQ2=makeQuery(id+"F0.imprint","INTERSECT",VERTEX,{"derivedFrom":[subQ1,subQ0]});Q19=makeQuery(id+"F0.imprint","IMPRINT",FACE,{"disambiguationData":[TD([[makeQuery(id+"F0.imprint","IMPRINT",EDGE,{"disambiguationData":[TD([[subQ2,1.0]])],"derivedFrom":subQ1}),-1.0]])]});}
            var Q20;
            {var subQ0=sQuery(id+"F0.wireOp",EDGE,"E93");Q20=makeQuery(id+"F0.imprint","IMPRINT",FACE,{"disambiguationData":[TD([[makeQuery(id+"F0.imprint","IMPRINT",EDGE,{"derivedFrom":subQ0}),1.0]])]});}
            var Q21;
            {var subQ0=sQuery(id+"F0.wireOp",EDGE,"E53");var subQ1=sQuery(id+"F0.wireOp",EDGE,"E36");var subQ2=makeQuery(id+"F0.imprint","INTERSECT",VERTEX,{"derivedFrom":[subQ1,subQ0]});Q21=makeQuery(id+"F0.imprint","IMPRINT",FACE,{"disambiguationData":[TD([[makeQuery(id+"F0.imprint","IMPRINT",EDGE,{"disambiguationData":[TD([[subQ2,1.0]])],"derivedFrom":subQ1}),-1.0]])]});}
            var Q22;
            {var subQ0=sQuery(id+"F0.wireOp",EDGE,"E175");Q22=makeQuery(id+"F0.imprint","IMPRINT",FACE,{"disambiguationData":[TD([[makeQuery(id+"F0.imprint","IMPRINT",EDGE,{"derivedFrom":subQ0}),1.0]])]});}
            var Q23;
            {var subQ0=sQuery(id+"F0.wireOp",EDGE,"E223");var subQ1=sQuery(id+"F0.wireOp",EDGE,"E8");var subQ2=makeQuery(id+"F0.imprint","INTERSECT",VERTEX,{"derivedFrom":[subQ1,subQ0]});Q23=makeQuery(id+"F0.imprint","IMPRINT",FACE,{"disambiguationData":[TD([[makeQuery(id+"F0.imprint","IMPRINT",EDGE,{"disambiguationData":[TD([[subQ2,-1.0]])],"derivedFrom":subQ1}),1.0]])]});}
            var Q24;
            {var subQ0=sQuery(id+"F0.wireOp",EDGE,"E240");var subQ1=sQuery(id+"F0.wireOp",EDGE,"E8");var subQ2=makeQuery(id+"F0.imprint","INTERSECT",VERTEX,{"derivedFrom":[subQ1,subQ0]});Q24=makeQuery(id+"F0.imprint","IMPRINT",FACE,{"disambiguationData":[TD([[makeQuery(id+"F0.imprint","IMPRINT",EDGE,{"disambiguationData":[TD([[subQ2,-1.0]])],"derivedFrom":subQ1}),-1.0]])]});}
            var Q25;
            {var subQ0=sQuery(id+"F0.wireOp",EDGE,"E232");var subQ1=sQuery(id+"F0.wireOp",EDGE,"E8");var subQ2=makeQuery(id+"F0.imprint","INTERSECT",VERTEX,{"derivedFrom":[subQ1,subQ0]});Q25=makeQuery(id+"F0.imprint","IMPRINT",FACE,{"disambiguationData":[TD([[makeQuery(id+"F0.imprint","IMPRINT",EDGE,{"disambiguationData":[TD([[subQ2,-1.0]])],"derivedFrom":subQ1}),-1.0]])]});}
            var Q26;
            {var subQ0=sQuery(id+"F0.wireOp",EDGE,"E236");var subQ1=sQuery(id+"F0.wireOp",EDGE,"E8");var subQ2=makeQuery(id+"F0.imprint","INTERSECT",VERTEX,{"derivedFrom":[subQ1,subQ0]});Q26=makeQuery(id+"F0.imprint","IMPRINT",FACE,{"disambiguationData":[TD([[makeQuery(id+"F0.imprint","IMPRINT",EDGE,{"disambiguationData":[TD([[subQ2,1.0]])],"derivedFrom":subQ1}),-1.0]])]});}
            var Q27;
            {var subQ0=sQuery(id+"F0.wireOp",EDGE,"E9");Q27=makeQuery(id+"F0.imprint","IMPRINT",FACE,{"disambiguationData":[TD([[makeQuery(id+"F0.imprint","IMPRINT",EDGE,{"derivedFrom":subQ0}),-1.0]])]});}
            var Q28;
            {var subQ0=sQuery(id+"F0.wireOp",EDGE,"E10");Q28=makeQuery(id+"F0.imprint","IMPRINT",FACE,{"disambiguationData":[TD([[makeQuery(id+"F0.imprint","IMPRINT",EDGE,{"derivedFrom":subQ0}),1.0]])]});}
            var Q29;
            {var subQ0=sQuery(id+"F0.wireOp",EDGE,"E3");Q29=makeQuery(id+"F0.imprint","IMPRINT",FACE,{"disambiguationData":[TD([[makeQuery(id+"F0.imprint","IMPRINT",EDGE,{"derivedFrom":subQ0}),-1.0]])]});}
            var Q30;
            {var subQ0=sQuery(id+"F0.wireOp",EDGE,"E7");Q30=makeQuery(id+"F0.imprint","IMPRINT",FACE,{"disambiguationData":[TD([[makeQuery(id+"F0.imprint","IMPRINT",EDGE,{"derivedFrom":subQ0}),-1.0]])]});}
            var Q31;
            {var subQ0=sQuery(id+"F0.wireOp",EDGE,"E5");Q31=makeQuery(id+"F0.imprint","IMPRINT",FACE,{"disambiguationData":[TD([[makeQuery(id+"F0.imprint","IMPRINT",EDGE,{"derivedFrom":subQ0}),-1.0]])]});}
            var Q32;
            {var subQ1=sQuery(id+"F0.wireOp",EDGE,"E220");Q32=makeQuery(id+"F0.imprint","IMPRINT",FACE,{"disambiguationData":[TD([[makeQuery(id+"F0.imprint","IMPRINT",EDGE,{"derivedFrom":subQ1}),1.0]])]});}
            var Q33;
            {var subQ3=sQuery(id+"F0.wireOp",EDGE,"E8");var subQ5=sQuery(id+"F0.wireOp",EDGE,"E233");var subQ6=makeQuery(id+"F0.imprint","INTERSECT",VERTEX,{"derivedFrom":[subQ3,subQ5]});Q33=makeQuery(id+"F0.imprint","IMPRINT",FACE,{"disambiguationData":[TD([[makeQuery(id+"F0.imprint","IMPRINT",EDGE,{"disambiguationData":[TD([[subQ6,-1.0]])],"derivedFrom":subQ3}),1.0]])]});}
            var Q34;
            {var subQ0=sQuery(id+"F0.wireOp",EDGE,"E1");Q34=makeQuery(id+"F0.imprint","IMPRINT",FACE,{"disambiguationData":[TD([[makeQuery(id+"F0.imprint","IMPRINT",EDGE,{"derivedFrom":subQ0}),-1.0]])]});}
            extrude(context, id + "F3", {"entities" : qUnion([Q0, Q1, Q2, Q3, Q4, Q5, Q6, Q7, Q8, Q9, Q10, Q11, Q12, Q13, Q14, Q15, Q16, Q17, Q18, Q19, Q20, Q21, Q22, Q23, Q24, Q25, Q26, Q27, Q28, Q29, Q30, Q31, Q32, Q33, Q34]), "operationType" : NewBodyOperationType.ADD, "depth" : 8.8 * mm, "offsetDistance" : 25.4 * mm});
        }
    });
